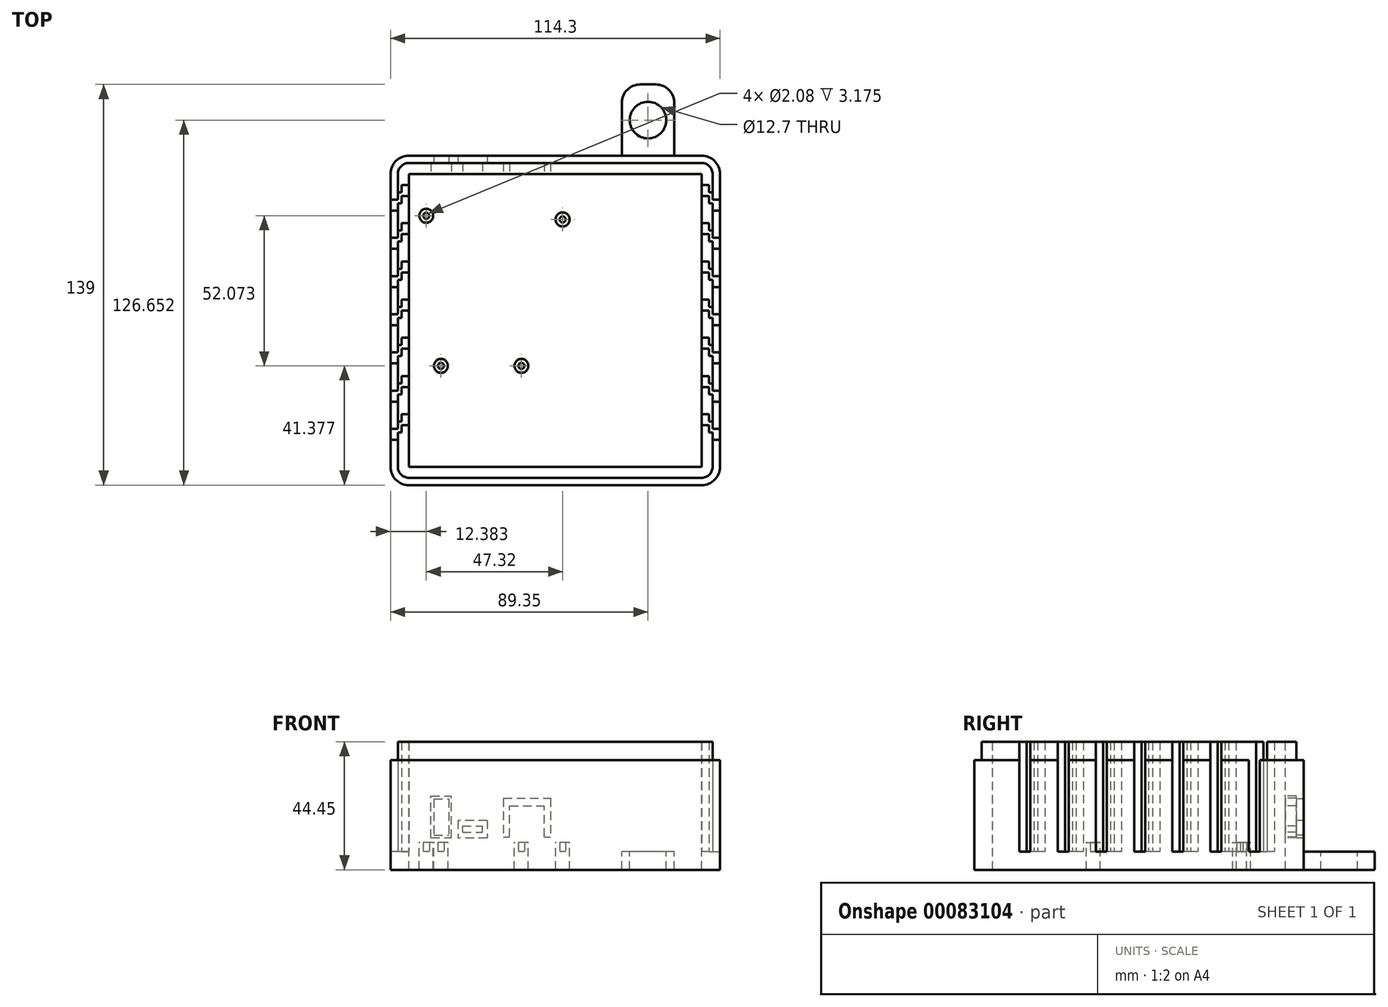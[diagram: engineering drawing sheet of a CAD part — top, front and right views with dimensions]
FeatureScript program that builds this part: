
annotation { "Feature Type Name" : "Feature", "Feature Type Description" : "" }
export const myFeature = defineFeature(function(context is Context, id is Id, definition is map)
    precondition{}
    {
        {
            var Q0;
            Q0=qCreatedBy(makeId("Top.planeOp"),FACE);
            var sketch = newSketch(context, id + "F0", { "sketchPlane" : qUnion([Q0])});
            skLineSegment(sketch, "E0.bottom", {"start": v(50.8, 57.15) * mm, "end": v(-50.8, 57.15) * mm});
            skLineSegment(sketch, "E0.top", {"start": v(50.8, -57.15) * mm, "end": v(-50.8, -57.15) * mm});
            skLineSegment(sketch, "E0.left", {"start": v(57.15, 50.8) * mm, "end": v(57.15, -50.8) * mm});
            skLineSegment(sketch, "E0.right", {"start": v(-57.15, 50.8) * mm, "end": v(-57.15, -50.8) * mm});
            skPoint(sketch, "E0.middle", {"position": v(0, 0) * mm});
            skPoint(sketch, "E1.visualSharp", {"position": v(57.15, 57.15) * mm});
            skArc(sketch, "E1.filletArc", {"start": v(57.15, 50.8) * mm, "mid": v(55.3, 55.3) * mm, "end": v(50.8, 57.15) * mm});
            skPoint(sketch, "E2.visualSharp", {"position": v(57.15, -57.15) * mm});
            skArc(sketch, "E2.filletArc", {"start": v(50.8, -57.15) * mm, "mid": v(55.3, -55.3) * mm, "end": v(57.15, -50.8) * mm});
            skPoint(sketch, "E3.visualSharp", {"position": v(-57.15, -57.15) * mm});
            skArc(sketch, "E3.filletArc", {"start": v(-57.15, -50.8) * mm, "mid": v(-55.3, -55.3) * mm, "end": v(-50.8, -57.15) * mm});
            skPoint(sketch, "E4.visualSharp", {"position": v(-57.15, 57.15) * mm});
            skArc(sketch, "E4.filletArc", {"start": v(-50.8, 57.15) * mm, "mid": v(-55.3, 55.3) * mm, "end": v(-57.15, 50.8) * mm});
            skLineSegment(sketch, "E5.bottom", {"start": v(-50.8, 50.8) * mm, "end": v(50.8, 50.8) * mm});
            skLineSegment(sketch, "E5.top", {"start": v(-50.8, -50.8) * mm, "end": v(50.8, -50.8) * mm});
            skLineSegment(sketch, "E5.left", {"start": v(-50.8, 50.8) * mm, "end": v(-50.8, -50.8) * mm});
            skLineSegment(sketch, "E5.right", {"start": v(50.8, 50.8) * mm, "end": v(50.8, -50.8) * mm});
            skCircle(sketch, "E6", {"center": v(32.2, 69.5) * mm, "radius": 6.35 * mm});
            skLineSegment(sketch, "E7.bottom", {"start": v(41.28, 57.15) * mm, "end": v(23.12, 57.15) * mm});
            skLineSegment(sketch, "E7.top", {"start": v(34.93, 81.85) * mm, "end": v(29.47, 81.85) * mm});
            skLineSegment(sketch, "E7.left", {"start": v(41.28, 57.15) * mm, "end": v(41.28, 75.5) * mm});
            skLineSegment(sketch, "E7.right", {"start": v(23.12, 57.15) * mm, "end": v(23.12, 75.5) * mm});
            skPoint(sketch, "E8.visualSharp", {"position": v(23.12, 81.85) * mm});
            skArc(sketch, "E8.filletArc", {"start": v(29.47, 81.85) * mm, "mid": v(24.98, 80) * mm, "end": v(23.12, 75.5) * mm});
            skPoint(sketch, "E9.visualSharp", {"position": v(41.28, 81.85) * mm});
            skArc(sketch, "E9.filletArc", {"start": v(41.28, 75.5) * mm, "mid": v(39.42, 80) * mm, "end": v(34.93, 81.85) * mm});
            skLineSegment(sketch, "E10.bottom", {"start": v(23.12, 57.15) * mm, "end": v(41.28, 57.15) * mm});
            skLineSegment(sketch, "E10.top", {"start": v(23.12, 50.8) * mm, "end": v(41.28, 50.8) * mm});
            skLineSegment(sketch, "E10.left", {"start": v(23.12, 57.15) * mm, "end": v(23.12, 50.8) * mm});
            skLineSegment(sketch, "E10.right", {"start": v(41.28, 57.15) * mm, "end": v(41.28, 50.8) * mm});
            skLineSegment(sketch, "E11.MirrorCS", {"start": v(23.12, -57.15) * mm, "end": v(23.12, -75.5) * mm});
            skArc(sketch, "E12.MirrorCS", {"start": v(29.47, -81.85) * mm, "mid": v(24.98, -80) * mm, "end": v(23.12, -75.5) * mm});
            skCircle(sketch, "E13.MirrorC", {"center": v(32.2, -69.5) * mm, "radius": 6.35 * mm});
            skLineSegment(sketch, "E14.MirrorCS", {"start": v(23.12, -57.15) * mm, "end": v(23.12, -50.8) * mm});
            skLineSegment(sketch, "E15.MirrorCS", {"start": v(41.28, -57.15) * mm, "end": v(41.28, -50.8) * mm});
            skLineSegment(sketch, "E16.MirrorCS", {"start": v(41.28, -57.15) * mm, "end": v(41.28, -75.5) * mm});
            skArc(sketch, "E17.MirrorCS", {"start": v(41.28, -75.5) * mm, "mid": v(39.42, -80) * mm, "end": v(34.93, -81.85) * mm});
            skLineSegment(sketch, "E18.MirrorCS", {"start": v(34.93, -81.85) * mm, "end": v(29.47, -81.85) * mm});
            skLineSegment(sketch, "E19", {"start": v(-50.8, 47.02) * mm, "end": v(-53.34, 47.02) * mm});
            skLineSegment(sketch, "E20", {"start": v(-53.34, 47.02) * mm, "end": v(-53.34, 44.48) * mm});
            skLineSegment(sketch, "E21", {"start": v(-53.34, 44.48) * mm, "end": v(-54.61, 44.48) * mm});
            skLineSegment(sketch, "E22", {"start": v(-54.61, 44.48) * mm, "end": v(-54.61, 41.94) * mm});
            skLineSegment(sketch, "E23", {"start": v(-54.61, 41.94) * mm, "end": v(-57.15, 41.94) * mm});
            skLineSegment(sketch, "E24", {"start": v(-50.8, 43.21) * mm, "end": v(-53.34, 43.21) * mm});
            skLineSegment(sketch, "E25", {"start": v(-53.34, 43.21) * mm, "end": v(-53.34, 40.67) * mm});
            skLineSegment(sketch, "E26", {"start": v(-53.34, 40.67) * mm, "end": v(-54.6, 40.67) * mm});
            skLineSegment(sketch, "E27", {"start": v(-54.6, 40.67) * mm, "end": v(-54.6, 38.13) * mm});
            skLineSegment(sketch, "E28", {"start": v(-54.6, 38.13) * mm, "end": v(-57.15, 38.13) * mm});
            skLineSegment(sketch, "E29.1.0.0", {"start": v(-53.34, 33.75) * mm, "end": v(-53.34, 31.21) * mm});
            skLineSegment(sketch, "E29.1.0.1", {"start": v(-53.34, 31.21) * mm, "end": v(-54.6, 31.21) * mm});
            skLineSegment(sketch, "E29.1.0.2", {"start": v(-54.6, 31.21) * mm, "end": v(-54.6, 28.67) * mm});
            skLineSegment(sketch, "E29.1.0.3", {"start": v(-53.34, 29.94) * mm, "end": v(-53.34, 27.4) * mm});
            skLineSegment(sketch, "E29.1.0.4", {"start": v(-53.34, 27.4) * mm, "end": v(-54.6, 27.4) * mm});
            skLineSegment(sketch, "E29.1.0.5", {"start": v(-54.6, 27.4) * mm, "end": v(-54.6, 24.86) * mm});
            skLineSegment(sketch, "E29.2.0.0", {"start": v(-53.34, 20.49) * mm, "end": v(-53.34, 17.95) * mm});
            skLineSegment(sketch, "E29.2.0.1", {"start": v(-53.34, 17.95) * mm, "end": v(-54.6, 17.95) * mm});
            skLineSegment(sketch, "E29.2.0.2", {"start": v(-54.6, 17.95) * mm, "end": v(-54.6, 15.4) * mm});
            skLineSegment(sketch, "E29.2.0.3", {"start": v(-53.34, 16.68) * mm, "end": v(-53.34, 14.14) * mm});
            skLineSegment(sketch, "E29.2.0.4", {"start": v(-53.34, 14.14) * mm, "end": v(-54.6, 14.14) * mm});
            skLineSegment(sketch, "E29.2.0.5", {"start": v(-54.6, 14.14) * mm, "end": v(-54.6, 11.6) * mm});
            skLineSegment(sketch, "E29.3.0.0", {"start": v(-53.33, 7.22) * mm, "end": v(-53.33, 4.68) * mm});
            skLineSegment(sketch, "E29.3.0.1", {"start": v(-53.33, 4.68) * mm, "end": v(-54.6, 4.68) * mm});
            skLineSegment(sketch, "E29.3.0.2", {"start": v(-54.6, 4.68) * mm, "end": v(-54.6, 2.14) * mm});
            skLineSegment(sketch, "E29.3.0.3", {"start": v(-53.33, 3.4) * mm, "end": v(-53.33, 0.87) * mm});
            skLineSegment(sketch, "E29.3.0.4", {"start": v(-53.33, 0.87) * mm, "end": v(-54.6, 0.87) * mm});
            skLineSegment(sketch, "E29.3.0.5", {"start": v(-54.6, 0.87) * mm, "end": v(-54.6, -1.67) * mm});
            skLineSegment(sketch, "E29.4.0.0", {"start": v(-53.33, -6.05) * mm, "end": v(-53.33, -8.6) * mm});
            skLineSegment(sketch, "E29.4.0.1", {"start": v(-53.33, -8.6) * mm, "end": v(-54.6, -8.6) * mm});
            skLineSegment(sketch, "E29.4.0.2", {"start": v(-54.6, -8.6) * mm, "end": v(-54.6, -11.13) * mm});
            skLineSegment(sketch, "E29.4.0.3", {"start": v(-53.33, -9.86) * mm, "end": v(-53.33, -12.4) * mm});
            skLineSegment(sketch, "E29.4.0.4", {"start": v(-53.33, -12.4) * mm, "end": v(-54.6, -12.4) * mm});
            skLineSegment(sketch, "E29.4.0.5", {"start": v(-54.6, -12.4) * mm, "end": v(-54.6, -14.94) * mm});
            skLineSegment(sketch, "E29.5.0.0", {"start": v(-53.33, -19.32) * mm, "end": v(-53.33, -21.86) * mm});
            skLineSegment(sketch, "E29.5.0.1", {"start": v(-53.33, -21.86) * mm, "end": v(-54.6, -21.86) * mm});
            skLineSegment(sketch, "E29.5.0.2", {"start": v(-54.6, -21.86) * mm, "end": v(-54.6, -24.4) * mm});
            skLineSegment(sketch, "E29.5.0.3", {"start": v(-53.33, -23.13) * mm, "end": v(-53.33, -25.67) * mm});
            skLineSegment(sketch, "E29.5.0.4", {"start": v(-53.33, -25.67) * mm, "end": v(-54.6, -25.67) * mm});
            skLineSegment(sketch, "E29.5.0.5", {"start": v(-54.6, -25.67) * mm, "end": v(-54.6, -28.2) * mm});
            skLineSegment(sketch, "E29.6.0.0", {"start": v(-53.33, -32.59) * mm, "end": v(-53.33, -35.13) * mm});
            skLineSegment(sketch, "E29.6.0.1", {"start": v(-53.33, -35.13) * mm, "end": v(-54.6, -35.13) * mm});
            skLineSegment(sketch, "E29.6.0.2", {"start": v(-54.6, -35.13) * mm, "end": v(-54.6, -37.67) * mm});
            skLineSegment(sketch, "E29.6.0.3", {"start": v(-53.33, -36.4) * mm, "end": v(-53.33, -38.94) * mm});
            skLineSegment(sketch, "E29.6.0.4", {"start": v(-53.33, -38.94) * mm, "end": v(-54.6, -38.94) * mm});
            skLineSegment(sketch, "E29.6.0.5", {"start": v(-54.6, -38.94) * mm, "end": v(-54.6, -41.48) * mm});
            skLineSegment(sketch, "E29.direction1", {"start": v(-53.34, 44.48) * mm, "end": v(-53.34, 31.21) * mm, "construction": true});
            skLineSegment(sketch, "E30", {"start": v(-53.34, 33.75) * mm, "end": v(-50.8, 33.75) * mm});
            skLineSegment(sketch, "E31", {"start": v(-53.34, 29.94) * mm, "end": v(-50.8, 29.94) * mm});
            skLineSegment(sketch, "E32", {"start": v(-54.6, 28.67) * mm, "end": v(-57.15, 28.67) * mm});
            skLineSegment(sketch, "E33", {"start": v(-54.6, 24.86) * mm, "end": v(-57.15, 24.86) * mm});
            skLineSegment(sketch, "E34", {"start": v(-53.34, 20.49) * mm, "end": v(-50.8, 20.49) * mm});
            skLineSegment(sketch, "E35", {"start": v(-53.34, 16.68) * mm, "end": v(-50.8, 16.68) * mm});
            skLineSegment(sketch, "E36", {"start": v(-54.6, 15.4) * mm, "end": v(-57.15, 15.4) * mm});
            skLineSegment(sketch, "E37", {"start": v(-54.6, 11.6) * mm, "end": v(-57.15, 11.6) * mm});
            skLineSegment(sketch, "E38", {"start": v(-53.33, 7.22) * mm, "end": v(-50.8, 7.22) * mm});
            skLineSegment(sketch, "E39", {"start": v(-53.33, 3.4) * mm, "end": v(-50.8, 3.4) * mm});
            skLineSegment(sketch, "E40", {"start": v(-54.6, 2.14) * mm, "end": v(-57.15, 2.14) * mm});
            skLineSegment(sketch, "E41", {"start": v(-54.6, -1.67) * mm, "end": v(-57.15, -1.67) * mm});
            skLineSegment(sketch, "E42", {"start": v(-53.33, -6.05) * mm, "end": v(-50.8, -6.05) * mm});
            skLineSegment(sketch, "E43", {"start": v(-53.33, -9.86) * mm, "end": v(-50.8, -9.86) * mm});
            skLineSegment(sketch, "E44", {"start": v(-53.33, -19.32) * mm, "end": v(-50.8, -19.32) * mm});
            skLineSegment(sketch, "E45", {"start": v(-53.33, -23.13) * mm, "end": v(-50.8, -23.13) * mm});
            skLineSegment(sketch, "E46", {"start": v(-53.33, -32.59) * mm, "end": v(-50.8, -32.59) * mm});
            skLineSegment(sketch, "E47", {"start": v(-53.33, -36.4) * mm, "end": v(-50.8, -36.4) * mm});
            skLineSegment(sketch, "E48", {"start": v(-54.6, -11.13) * mm, "end": v(-57.15, -11.13) * mm});
            skLineSegment(sketch, "E49", {"start": v(-54.6, -14.94) * mm, "end": v(-57.15, -14.94) * mm});
            skLineSegment(sketch, "E50", {"start": v(-54.6, -24.4) * mm, "end": v(-57.15, -24.4) * mm});
            skLineSegment(sketch, "E51", {"start": v(-54.6, -28.2) * mm, "end": v(-57.15, -28.2) * mm});
            skLineSegment(sketch, "E52", {"start": v(-54.6, -37.67) * mm, "end": v(-57.15, -37.67) * mm});
            skLineSegment(sketch, "E53", {"start": v(-54.6, -41.48) * mm, "end": v(-57.15, -41.48) * mm});
            skLineSegment(sketch, "E54.MirrorCS", {"start": v(54.6, -38.94) * mm, "end": v(54.6, -41.48) * mm});
            skLineSegment(sketch, "E55.MirrorCS", {"start": v(53.33, -38.94) * mm, "end": v(54.6, -38.94) * mm});
            skLineSegment(sketch, "E56.MirrorCS", {"start": v(53.33, -36.4) * mm, "end": v(53.33, -38.94) * mm});
            skLineSegment(sketch, "E57.MirrorCS", {"start": v(54.6, -35.13) * mm, "end": v(54.6, -37.67) * mm});
            skLineSegment(sketch, "E58.MirrorCS", {"start": v(53.33, -35.13) * mm, "end": v(54.6, -35.13) * mm});
            skLineSegment(sketch, "E59.MirrorCS", {"start": v(53.33, -32.59) * mm, "end": v(53.33, -35.13) * mm});
            skLineSegment(sketch, "E60.MirrorCS", {"start": v(54.6, -25.67) * mm, "end": v(54.6, -28.2) * mm});
            skLineSegment(sketch, "E61.MirrorCS", {"start": v(53.33, -25.67) * mm, "end": v(54.6, -25.67) * mm});
            skLineSegment(sketch, "E62.MirrorCS", {"start": v(53.33, -23.13) * mm, "end": v(53.33, -25.67) * mm});
            skLineSegment(sketch, "E63.MirrorCS", {"start": v(54.6, -21.86) * mm, "end": v(54.6, -24.4) * mm});
            skLineSegment(sketch, "E64.MirrorCS", {"start": v(53.33, -21.86) * mm, "end": v(54.6, -21.86) * mm});
            skLineSegment(sketch, "E65.MirrorCS", {"start": v(53.33, -19.32) * mm, "end": v(53.33, -21.86) * mm});
            skLineSegment(sketch, "E66.MirrorCS", {"start": v(54.6, -12.4) * mm, "end": v(54.6, -14.94) * mm});
            skLineSegment(sketch, "E67.MirrorCS", {"start": v(53.33, -12.4) * mm, "end": v(54.6, -12.4) * mm});
            skLineSegment(sketch, "E68.MirrorCS", {"start": v(53.33, -9.86) * mm, "end": v(53.33, -12.4) * mm});
            skLineSegment(sketch, "E69.MirrorCS", {"start": v(54.6, -8.6) * mm, "end": v(54.6, -11.13) * mm});
            skLineSegment(sketch, "E70.MirrorCS", {"start": v(53.33, -8.6) * mm, "end": v(54.6, -8.6) * mm});
            skLineSegment(sketch, "E71.MirrorCS", {"start": v(53.33, -6.05) * mm, "end": v(53.33, -8.6) * mm});
            skLineSegment(sketch, "E72.MirrorCS", {"start": v(54.6, 0.87) * mm, "end": v(54.6, -1.67) * mm});
            skLineSegment(sketch, "E73.MirrorCS", {"start": v(53.33, 0.87) * mm, "end": v(54.6, 0.87) * mm});
            skLineSegment(sketch, "E74.MirrorCS", {"start": v(53.33, 3.4) * mm, "end": v(53.33, 0.87) * mm});
            skLineSegment(sketch, "E75.MirrorCS", {"start": v(54.6, 4.68) * mm, "end": v(54.6, 2.14) * mm});
            skLineSegment(sketch, "E76.MirrorCS", {"start": v(53.33, 4.68) * mm, "end": v(54.6, 4.68) * mm});
            skLineSegment(sketch, "E77.MirrorCS", {"start": v(53.33, 7.22) * mm, "end": v(53.33, 4.68) * mm});
            skLineSegment(sketch, "E78.MirrorCS", {"start": v(53.34, 44.48) * mm, "end": v(54.61, 44.48) * mm});
            skLineSegment(sketch, "E79.MirrorCS", {"start": v(54.61, 44.48) * mm, "end": v(54.61, 41.94) * mm});
            skLineSegment(sketch, "E80.MirrorCS", {"start": v(54.6, 40.67) * mm, "end": v(54.6, 38.13) * mm});
            skLineSegment(sketch, "E81.MirrorCS", {"start": v(53.34, 40.67) * mm, "end": v(54.6, 40.67) * mm});
            skLineSegment(sketch, "E82.MirrorCS", {"start": v(53.34, 43.21) * mm, "end": v(53.34, 40.67) * mm});
            skLineSegment(sketch, "E83.MirrorCS", {"start": v(53.34, 47.02) * mm, "end": v(53.34, 44.48) * mm});
            skLineSegment(sketch, "E84.MirrorCS", {"start": v(54.6, 14.14) * mm, "end": v(54.6, 11.6) * mm});
            skLineSegment(sketch, "E85.MirrorCS", {"start": v(53.34, 14.14) * mm, "end": v(54.6, 14.14) * mm});
            skLineSegment(sketch, "E86.MirrorCS", {"start": v(53.34, 16.68) * mm, "end": v(53.34, 14.14) * mm});
            skLineSegment(sketch, "E87.MirrorCS", {"start": v(54.6, 17.95) * mm, "end": v(54.6, 15.4) * mm});
            skLineSegment(sketch, "E88.MirrorCS", {"start": v(53.34, 17.95) * mm, "end": v(54.6, 17.95) * mm});
            skLineSegment(sketch, "E89.MirrorCS", {"start": v(53.34, 20.49) * mm, "end": v(53.34, 17.95) * mm});
            skLineSegment(sketch, "E90.MirrorCS", {"start": v(54.6, 27.4) * mm, "end": v(54.6, 24.86) * mm});
            skLineSegment(sketch, "E91.MirrorCS", {"start": v(53.34, 27.4) * mm, "end": v(54.6, 27.4) * mm});
            skLineSegment(sketch, "E92.MirrorCS", {"start": v(54.6, 31.21) * mm, "end": v(54.6, 28.67) * mm});
            skLineSegment(sketch, "E93.MirrorCS", {"start": v(53.34, 31.21) * mm, "end": v(54.6, 31.21) * mm});
            skLineSegment(sketch, "E94.MirrorCS", {"start": v(53.34, 29.94) * mm, "end": v(53.34, 27.4) * mm});
            skLineSegment(sketch, "E95.MirrorCS", {"start": v(53.34, 33.75) * mm, "end": v(53.34, 31.21) * mm});
            skLineSegment(sketch, "E96", {"start": v(53.34, 47.02) * mm, "end": v(50.8, 47.02) * mm});
            skLineSegment(sketch, "E97", {"start": v(53.34, 43.21) * mm, "end": v(50.8, 43.21) * mm});
            skLineSegment(sketch, "E98", {"start": v(54.61, 41.94) * mm, "end": v(57.15, 41.94) * mm});
            skLineSegment(sketch, "E99", {"start": v(54.6, 38.13) * mm, "end": v(57.15, 38.13) * mm});
            skLineSegment(sketch, "E100", {"start": v(53.34, 29.94) * mm, "end": v(50.8, 29.94) * mm});
            skLineSegment(sketch, "E101", {"start": v(54.6, 24.86) * mm, "end": v(57.15, 24.86) * mm});
            skLineSegment(sketch, "E102", {"start": v(53.34, 20.49) * mm, "end": v(50.8, 20.49) * mm});
            skLineSegment(sketch, "E103", {"start": v(53.34, 16.68) * mm, "end": v(50.8, 16.68) * mm});
            skLineSegment(sketch, "E104", {"start": v(54.6, 15.4) * mm, "end": v(57.15, 15.4) * mm});
            skLineSegment(sketch, "E105", {"start": v(54.6, 11.6) * mm, "end": v(57.15, 11.6) * mm});
            skLineSegment(sketch, "E106", {"start": v(53.33, 7.22) * mm, "end": v(50.8, 7.22) * mm});
            skLineSegment(sketch, "E107", {"start": v(53.33, 3.4) * mm, "end": v(50.8, 3.4) * mm});
            skLineSegment(sketch, "E108", {"start": v(54.6, 2.14) * mm, "end": v(57.15, 2.14) * mm});
            skLineSegment(sketch, "E109", {"start": v(54.6, -1.67) * mm, "end": v(57.15, -1.67) * mm});
            skLineSegment(sketch, "E110", {"start": v(53.33, -6.05) * mm, "end": v(50.8, -6.05) * mm});
            skLineSegment(sketch, "E111", {"start": v(53.33, -9.86) * mm, "end": v(50.8, -9.86) * mm});
            skLineSegment(sketch, "E112", {"start": v(54.6, -11.13) * mm, "end": v(57.15, -11.13) * mm});
            skLineSegment(sketch, "E113", {"start": v(54.6, -14.94) * mm, "end": v(57.15, -14.94) * mm});
            skLineSegment(sketch, "E114", {"start": v(53.33, -19.32) * mm, "end": v(50.8, -19.32) * mm});
            skLineSegment(sketch, "E115", {"start": v(53.33, -23.13) * mm, "end": v(50.8, -23.13) * mm});
            skLineSegment(sketch, "E116", {"start": v(54.6, -24.4) * mm, "end": v(57.15, -24.4) * mm});
            skLineSegment(sketch, "E117", {"start": v(54.6, -28.2) * mm, "end": v(57.15, -28.2) * mm});
            skLineSegment(sketch, "E118", {"start": v(53.33, -32.59) * mm, "end": v(50.8, -32.59) * mm});
            skLineSegment(sketch, "E119", {"start": v(53.33, -36.4) * mm, "end": v(50.8, -36.4) * mm});
            skLineSegment(sketch, "E120", {"start": v(54.6, -37.67) * mm, "end": v(57.15, -37.67) * mm});
            skLineSegment(sketch, "E121", {"start": v(54.6, -41.48) * mm, "end": v(57.15, -41.48) * mm});
            skLineSegment(sketch, "E122", {"start": v(53.34, 33.75) * mm, "end": v(50.8, 33.75) * mm});
            skLineSegment(sketch, "E123", {"start": v(54.6, 28.67) * mm, "end": v(57.15, 28.67) * mm});
            skLineSegment(sketch, "E124", {"start": v(54.61, -50.8) * mm, "end": v(54.61, 50.8) * mm});
            skLineSegment(sketch, "E125", {"start": v(-54.61, -50.8) * mm, "end": v(-54.61, 50.8) * mm});
            skLineSegment(sketch, "E126", {"start": v(-50.8, 54.61) * mm, "end": v(50.8, 54.61) * mm});
            skArc(sketch, "E127", {"start": v(-50.8, 54.6) * mm, "mid": v(-53.5, 53.5) * mm, "end": v(-54.61, 50.8) * mm});
            skArc(sketch, "E128", {"start": v(50.8, 54.61) * mm, "mid": v(53.5, 53.5) * mm, "end": v(54.6, 50.8) * mm});
            skArc(sketch, "E129", {"start": v(54.61, -50.8) * mm, "mid": v(53.5, -53.5) * mm, "end": v(50.8, -54.61) * mm});
            skArc(sketch, "E130", {"start": v(-54.61, -50.8) * mm, "mid": v(-53.5, -53.5) * mm, "end": v(-50.8, -54.61) * mm});
            skLineSegment(sketch, "E131", {"start": v(-50.8, -54.61) * mm, "end": v(50.8, -54.61) * mm});
            skCircle(sketch, "E132", {"center": v(-44.77, 36.3) * mm, "radius": 1.04 * mm});
            skCircle(sketch, "E133", {"center": v(-44.77, 36.3) * mm, "radius": 2.42 * mm});
            skCircle(sketch, "E134", {"center": v(2.55, 35.03) * mm, "radius": 1.04 * mm});
            skCircle(sketch, "E135", {"center": v(2.55, 35.03) * mm, "radius": 2.42 * mm});
            skCircle(sketch, "E136", {"center": v(-39.67, -15.77) * mm, "radius": 1.04 * mm});
            skCircle(sketch, "E137", {"center": v(-39.67, -15.77) * mm, "radius": 2.42 * mm});
            skCircle(sketch, "E138", {"center": v(-11.73, -15.77) * mm, "radius": 1.04 * mm});
            skCircle(sketch, "E139", {"center": v(-11.73, -15.77) * mm, "radius": 2.42 * mm});
            skSolve(sketch);
        }
        {
            var Q0;
            {var subQ5=sQuery(id+"F0.wireOp",EDGE,"E4.filletArc");Q0=makeQuery(id+"F0.imprint","IMPRINT",FACE,{"disambiguationData":[TD([[makeQuery(id+"F0.imprint","IMPRINT",EDGE,{"derivedFrom":subQ5}),1.0]])]});}
            var Q1;
            {var subQ0=sQuery(id+"F0.wireOp",EDGE,"E19");Q1=makeQuery(id+"F0.imprint","IMPRINT",FACE,{"disambiguationData":[TD([[makeQuery(id+"F0.imprint","IMPRINT",EDGE,{"derivedFrom":subQ0}),-1.0]])]});}
            var Q2;
            {var subQ0=sQuery(id+"F0.wireOp",EDGE,"7fccda47-ab33-4617-952b-09ef6f2d93c20.MirrorCS");var subQ1=sQuery(id+"F0.wireOp",EDGE,"E5.bottom");var subQ2=makeQuery(id+"F0.imprint","INTERSECT",VERTEX,{"derivedFrom":[subQ1,subQ0]});Q2=makeQuery(id+"F0.imprint","IMPRINT",FACE,{"disambiguationData":[TD([[makeQuery(id+"F0.imprint","IMPRINT",EDGE,{"disambiguationData":[TD([[subQ2,1.0]])],"derivedFrom":subQ1}),1.0]])]});}
            var Q3;
            {var subQ0=sQuery(id+"F0.wireOp",EDGE,"7fccda47-ab33-4617-952b-09ef6f2d93c20.MirrorCS");var subQ5=sQuery(id+"F0.wireOp",EDGE,"E126");var subQ6=makeQuery(id+"F0.imprint","INTERSECT",VERTEX,{"derivedFrom":[subQ0,subQ5]});Q3=makeQuery(id+"F0.imprint","IMPRINT",FACE,{"disambiguationData":[TD([[makeQuery(id+"F0.imprint","IMPRINT",EDGE,{"disambiguationData":[TD([[subQ6,1.0]])],"derivedFrom":subQ5}),1.0]])]});}
            var Q4;
            {var subQ1=sQuery(id+"F0.wireOp",EDGE,"f4708bc4-65f7-4d25-ab76-2e2c8adc8cc10.MirrorCS");Q4=makeQuery(id+"F0.imprint","IMPRINT",FACE,{"disambiguationData":[TD([[makeQuery(id+"F0.imprint","IMPRINT",EDGE,{"derivedFrom":subQ1}),1.0]])]});}
            var Q5;
            {var subQ0=sQuery(id+"F0.wireOp",EDGE,"E10.left");var subQ5=sQuery(id+"F0.wireOp",EDGE,"E126");var subQ6=makeQuery(id+"F0.imprint","INTERSECT",VERTEX,{"derivedFrom":[subQ0,subQ5]});Q5=makeQuery(id+"F0.imprint","IMPRINT",FACE,{"disambiguationData":[TD([[makeQuery(id+"F0.imprint","IMPRINT",EDGE,{"disambiguationData":[TD([[subQ6,1.0]])],"derivedFrom":subQ5}),1.0]])]});}
            var Q6;
            {var subQ1=sQuery(id+"F0.wireOp",EDGE,"E5.bottom");var subQ3=sQuery(id+"F0.wireOp",EDGE,"7fccda47-ab33-4617-952b-09ef6f2d93c20.MirrorCS");var subQ4=makeQuery(id+"F0.imprint","INTERSECT",VERTEX,{"derivedFrom":[subQ1,subQ3]});Q6=makeQuery(id+"F0.imprint","IMPRINT",FACE,{"disambiguationData":[TD([[makeQuery(id+"F0.imprint","IMPRINT",EDGE,{"disambiguationData":[TD([[subQ4,1.0]])],"derivedFrom":subQ3}),1.0]])]});}
            var Q7;
            {var subQ0=sQuery(id+"F0.wireOp",EDGE,"E10.top");Q7=makeQuery(id+"F0.imprint","IMPRINT",FACE,{"disambiguationData":[TD([[makeQuery(id+"F0.imprint","IMPRINT",EDGE,{"derivedFrom":subQ0}),1.0]])]});}
            var Q8;
            {var subQ0=sQuery(id+"F0.wireOp",EDGE,"E10.bottom");Q8=makeQuery(id+"F0.imprint","IMPRINT",FACE,{"disambiguationData":[TD([[makeQuery(id+"F0.imprint","IMPRINT",EDGE,{"derivedFrom":subQ0}),-1.0]])]});}
            var Q9;
            Q9=makeQuery(id+"F0.imprint","IMPRINT",FACE,{"disambiguationData":[TD([[makeQuery(id+"F0.imprint","IMPRINT",EDGE,{"derivedFrom":sQuery(id+"F0.wireOp",EDGE,"E6")}),-1.0]])]});
            var Q10;
            {var subQ8=sQuery(id+"F0.wireOp",EDGE,"E1.filletArc");Q10=makeQuery(id+"F0.imprint","IMPRINT",FACE,{"disambiguationData":[TD([[makeQuery(id+"F0.imprint","IMPRINT",EDGE,{"derivedFrom":subQ8}),1.0]])]});}
            var Q11;
            Q11=makeQuery(id+"F0.imprint","IMPRINT",FACE,{"disambiguationData":[TD([[makeQuery(id+"F0.imprint","IMPRINT",EDGE,{"derivedFrom":sQuery(id+"F0.wireOp",EDGE,"E83.MirrorCS")}),1.0]])]});
            var Q12;
            Q12=makeQuery(id+"F0.imprint","IMPRINT",FACE,{"disambiguationData":[TD([[makeQuery(id+"F0.imprint","IMPRINT",EDGE,{"derivedFrom":sQuery(id+"F0.wireOp",EDGE,"E83.MirrorCS")}),-1.0]])]});
            var Q13;
            {var subQ3=sQuery(id+"F0.wireOp",EDGE,"E98");Q13=makeQuery(id+"F0.imprint","IMPRINT",FACE,{"disambiguationData":[TD([[makeQuery(id+"F0.imprint","IMPRINT",EDGE,{"derivedFrom":subQ3}),-1.0]])]});}
            var Q14;
            {var subQ0=sQuery(id+"F0.wireOp",EDGE,"E99");Q14=makeQuery(id+"F0.imprint","IMPRINT",FACE,{"disambiguationData":[TD([[makeQuery(id+"F0.imprint","IMPRINT",EDGE,{"derivedFrom":subQ0}),-1.0]])]});}
            var Q15;
            Q15=makeQuery(id+"F0.imprint","IMPRINT",FACE,{"disambiguationData":[TD([[makeQuery(id+"F0.imprint","IMPRINT",EDGE,{"derivedFrom":sQuery(id+"F0.wireOp",EDGE,"E82.MirrorCS")}),-1.0]])]});
            var Q16;
            Q16=makeQuery(id+"F0.imprint","IMPRINT",FACE,{"disambiguationData":[TD([[makeQuery(id+"F0.imprint","IMPRINT",EDGE,{"derivedFrom":sQuery(id+"F0.wireOp",EDGE,"E95.MirrorCS")}),-1.0]])]});
            var Q17;
            {var subQ0=sQuery(id+"F0.wireOp",EDGE,"E101");var subQ1=sQuery(id+"F0.wireOp",EDGE,"E0.left");var subQ2=makeQuery(id+"F0.imprint","INTERSECT",VERTEX,{"derivedFrom":[subQ1,subQ0]});Q17=makeQuery(id+"F0.imprint","IMPRINT",FACE,{"disambiguationData":[TD([[makeQuery(id+"F0.imprint","IMPRINT",EDGE,{"disambiguationData":[TD([[subQ2,1.0]])],"derivedFrom":subQ1}),-1.0]])]});}
            var Q18;
            {var subQ0=sQuery(id+"F0.wireOp",EDGE,"E101");var subQ1=sQuery(id+"F0.wireOp",EDGE,"E0.left");var subQ2=makeQuery(id+"F0.imprint","INTERSECT",VERTEX,{"derivedFrom":[subQ1,subQ0]});Q18=makeQuery(id+"F0.imprint","IMPRINT",FACE,{"disambiguationData":[TD([[makeQuery(id+"F0.imprint","IMPRINT",EDGE,{"disambiguationData":[TD([[subQ2,-1.0]])],"derivedFrom":subQ1}),-1.0]])]});}
            var Q19;
            {var subQ6=sQuery(id+"F0.wireOp",EDGE,"E87.MirrorCS");Q19=makeQuery(id+"F0.imprint","IMPRINT",FACE,{"disambiguationData":[TD([[makeQuery(id+"F0.imprint","IMPRINT",EDGE,{"derivedFrom":subQ6}),1.0]])]});}
            var Q20;
            {var subQ7=sQuery(id+"F0.wireOp",EDGE,"E84.MirrorCS");Q20=makeQuery(id+"F0.imprint","IMPRINT",FACE,{"disambiguationData":[TD([[makeQuery(id+"F0.imprint","IMPRINT",EDGE,{"derivedFrom":subQ7}),1.0]])]});}
            var Q21;
            {var subQ0=sQuery(id+"F0.wireOp",EDGE,"E104");var subQ1=sQuery(id+"F0.wireOp",EDGE,"E0.left");var subQ2=makeQuery(id+"F0.imprint","INTERSECT",VERTEX,{"derivedFrom":[subQ1,subQ0]});Q21=makeQuery(id+"F0.imprint","IMPRINT",FACE,{"disambiguationData":[TD([[makeQuery(id+"F0.imprint","IMPRINT",EDGE,{"disambiguationData":[TD([[subQ2,-1.0]])],"derivedFrom":subQ1}),-1.0]])]});}
            var Q22;
            {var subQ8=sQuery(id+"F0.wireOp",EDGE,"E75.MirrorCS");Q22=makeQuery(id+"F0.imprint","IMPRINT",FACE,{"disambiguationData":[TD([[makeQuery(id+"F0.imprint","IMPRINT",EDGE,{"derivedFrom":subQ8}),1.0]])]});}
            var Q23;
            {var subQ0=sQuery(id+"F0.wireOp",EDGE,"E105");var subQ1=sQuery(id+"F0.wireOp",EDGE,"E0.left");var subQ2=makeQuery(id+"F0.imprint","INTERSECT",VERTEX,{"derivedFrom":[subQ1,subQ0]});Q23=makeQuery(id+"F0.imprint","IMPRINT",FACE,{"disambiguationData":[TD([[makeQuery(id+"F0.imprint","IMPRINT",EDGE,{"disambiguationData":[TD([[subQ2,-1.0]])],"derivedFrom":subQ1}),-1.0]])]});}
            var Q24;
            {var subQ0=sQuery(id+"F0.wireOp",EDGE,"E108");var subQ1=sQuery(id+"F0.wireOp",EDGE,"E0.left");var subQ2=makeQuery(id+"F0.imprint","INTERSECT",VERTEX,{"derivedFrom":[subQ1,subQ0]});Q24=makeQuery(id+"F0.imprint","IMPRINT",FACE,{"disambiguationData":[TD([[makeQuery(id+"F0.imprint","IMPRINT",EDGE,{"disambiguationData":[TD([[subQ2,-1.0]])],"derivedFrom":subQ1}),-1.0]])]});}
            var Q25;
            {var subQ6=sQuery(id+"F0.wireOp",EDGE,"E72.MirrorCS");Q25=makeQuery(id+"F0.imprint","IMPRINT",FACE,{"disambiguationData":[TD([[makeQuery(id+"F0.imprint","IMPRINT",EDGE,{"derivedFrom":subQ6}),1.0]])]});}
            var Q26;
            {var subQ6=sQuery(id+"F0.wireOp",EDGE,"E69.MirrorCS");Q26=makeQuery(id+"F0.imprint","IMPRINT",FACE,{"disambiguationData":[TD([[makeQuery(id+"F0.imprint","IMPRINT",EDGE,{"derivedFrom":subQ6}),1.0]])]});}
            var Q27;
            {var subQ0=sQuery(id+"F0.wireOp",EDGE,"E109");var subQ1=sQuery(id+"F0.wireOp",EDGE,"E0.left");var subQ2=makeQuery(id+"F0.imprint","INTERSECT",VERTEX,{"derivedFrom":[subQ1,subQ0]});Q27=makeQuery(id+"F0.imprint","IMPRINT",FACE,{"disambiguationData":[TD([[makeQuery(id+"F0.imprint","IMPRINT",EDGE,{"disambiguationData":[TD([[subQ2,-1.0]])],"derivedFrom":subQ1}),-1.0]])]});}
            var Q28;
            {var subQ9=sQuery(id+"F0.wireOp",EDGE,"E66.MirrorCS");Q28=makeQuery(id+"F0.imprint","IMPRINT",FACE,{"disambiguationData":[TD([[makeQuery(id+"F0.imprint","IMPRINT",EDGE,{"derivedFrom":subQ9}),1.0]])]});}
            var Q29;
            {var subQ0=sQuery(id+"F0.wireOp",EDGE,"E112");var subQ1=sQuery(id+"F0.wireOp",EDGE,"E0.left");var subQ2=makeQuery(id+"F0.imprint","INTERSECT",VERTEX,{"derivedFrom":[subQ1,subQ0]});Q29=makeQuery(id+"F0.imprint","IMPRINT",FACE,{"disambiguationData":[TD([[makeQuery(id+"F0.imprint","IMPRINT",EDGE,{"disambiguationData":[TD([[subQ2,-1.0]])],"derivedFrom":subQ1}),-1.0]])]});}
            var Q30;
            {var subQ0=sQuery(id+"F0.wireOp",EDGE,"E113");var subQ1=sQuery(id+"F0.wireOp",EDGE,"E0.left");var subQ2=makeQuery(id+"F0.imprint","INTERSECT",VERTEX,{"derivedFrom":[subQ1,subQ0]});Q30=makeQuery(id+"F0.imprint","IMPRINT",FACE,{"disambiguationData":[TD([[makeQuery(id+"F0.imprint","IMPRINT",EDGE,{"disambiguationData":[TD([[subQ2,-1.0]])],"derivedFrom":subQ1}),-1.0]])]});}
            var Q31;
            {var subQ7=sQuery(id+"F0.wireOp",EDGE,"E63.MirrorCS");Q31=makeQuery(id+"F0.imprint","IMPRINT",FACE,{"disambiguationData":[TD([[makeQuery(id+"F0.imprint","IMPRINT",EDGE,{"derivedFrom":subQ7}),1.0]])]});}
            var Q32;
            {var subQ8=sQuery(id+"F0.wireOp",EDGE,"E60.MirrorCS");Q32=makeQuery(id+"F0.imprint","IMPRINT",FACE,{"disambiguationData":[TD([[makeQuery(id+"F0.imprint","IMPRINT",EDGE,{"derivedFrom":subQ8}),1.0]])]});}
            var Q33;
            {var subQ0=sQuery(id+"F0.wireOp",EDGE,"E116");var subQ1=sQuery(id+"F0.wireOp",EDGE,"E0.left");var subQ2=makeQuery(id+"F0.imprint","INTERSECT",VERTEX,{"derivedFrom":[subQ1,subQ0]});Q33=makeQuery(id+"F0.imprint","IMPRINT",FACE,{"disambiguationData":[TD([[makeQuery(id+"F0.imprint","IMPRINT",EDGE,{"disambiguationData":[TD([[subQ2,-1.0]])],"derivedFrom":subQ1}),-1.0]])]});}
            var Q34;
            {var subQ0=sQuery(id+"F0.wireOp",EDGE,"E117");var subQ1=sQuery(id+"F0.wireOp",EDGE,"E0.left");var subQ2=makeQuery(id+"F0.imprint","INTERSECT",VERTEX,{"derivedFrom":[subQ1,subQ0]});Q34=makeQuery(id+"F0.imprint","IMPRINT",FACE,{"disambiguationData":[TD([[makeQuery(id+"F0.imprint","IMPRINT",EDGE,{"disambiguationData":[TD([[subQ2,-1.0]])],"derivedFrom":subQ1}),-1.0]])]});}
            var Q35;
            {var subQ7=sQuery(id+"F0.wireOp",EDGE,"E57.MirrorCS");Q35=makeQuery(id+"F0.imprint","IMPRINT",FACE,{"disambiguationData":[TD([[makeQuery(id+"F0.imprint","IMPRINT",EDGE,{"derivedFrom":subQ7}),1.0]])]});}
            var Q36;
            {var subQ7=sQuery(id+"F0.wireOp",EDGE,"E54.MirrorCS");Q36=makeQuery(id+"F0.imprint","IMPRINT",FACE,{"disambiguationData":[TD([[makeQuery(id+"F0.imprint","IMPRINT",EDGE,{"derivedFrom":subQ7}),1.0]])]});}
            var Q37;
            {var subQ0=sQuery(id+"F0.wireOp",EDGE,"E120");var subQ1=sQuery(id+"F0.wireOp",EDGE,"E0.left");var subQ2=makeQuery(id+"F0.imprint","INTERSECT",VERTEX,{"derivedFrom":[subQ1,subQ0]});Q37=makeQuery(id+"F0.imprint","IMPRINT",FACE,{"disambiguationData":[TD([[makeQuery(id+"F0.imprint","IMPRINT",EDGE,{"disambiguationData":[TD([[subQ2,-1.0]])],"derivedFrom":subQ1}),-1.0]])]});}
            var Q38;
            {var subQ0=sQuery(id+"F0.wireOp",EDGE,"E121");var subQ1=sQuery(id+"F0.wireOp",EDGE,"E0.left");var subQ2=makeQuery(id+"F0.imprint","INTERSECT",VERTEX,{"derivedFrom":[subQ1,subQ0]});Q38=makeQuery(id+"F0.imprint","IMPRINT",FACE,{"disambiguationData":[TD([[makeQuery(id+"F0.imprint","IMPRINT",EDGE,{"disambiguationData":[TD([[subQ2,-1.0]])],"derivedFrom":subQ1}),-1.0]])]});}
            var Q39;
            {var subQ7=sQuery(id+"F0.wireOp",EDGE,"859455d8-9afb-47e5-a04d-dad7f7b3347415.MirrorCS");Q39=makeQuery(id+"F0.imprint","IMPRINT",FACE,{"disambiguationData":[TD([[makeQuery(id+"F0.imprint","IMPRINT",EDGE,{"derivedFrom":subQ7}),1.0]])]});}
            var Q40;
            Q40=makeQuery(id+"F0.imprint","IMPRINT",FACE,{"disambiguationData":[TD([[makeQuery(id+"F0.imprint","IMPRINT",EDGE,{"derivedFrom":sQuery(id+"F0.wireOp",EDGE,"859455d8-9afb-47e5-a04d-dad7f7b3347412.MirrorCS")}),1.0]])]});
            var Q41;
            {var subQ0=sQuery(id+"F0.wireOp",EDGE,"PCcy3vUJ-A1Sm-yILS-TfP7-LZ45dRfwLIWC");var subQ1=sQuery(id+"F0.wireOp",EDGE,"E0.left");var subQ2=makeQuery(id+"F0.imprint","INTERSECT",VERTEX,{"derivedFrom":[subQ1,subQ0]});Q41=makeQuery(id+"F0.imprint","IMPRINT",FACE,{"disambiguationData":[TD([[makeQuery(id+"F0.imprint","IMPRINT",EDGE,{"disambiguationData":[TD([[subQ2,-1.0]])],"derivedFrom":subQ1}),-1.0]])]});}
            var Q42;
            {var subQ3=sQuery(id+"F0.wireOp",EDGE,"859455d8-9afb-47e5-a04d-dad7f7b334749.MirrorCS");Q42=makeQuery(id+"F0.imprint","IMPRINT",FACE,{"disambiguationData":[TD([[makeQuery(id+"F0.imprint","IMPRINT",EDGE,{"derivedFrom":subQ3}),1.0]])]});}
            var Q43;
            {var subQ0=sQuery(id+"F0.wireOp",EDGE,"SMXw2df1-MZSw-PhrQ-Zi49-mZn6oChbaFUW");var subQ1=sQuery(id+"F0.wireOp",EDGE,"E0.left");var subQ2=makeQuery(id+"F0.imprint","INTERSECT",VERTEX,{"derivedFrom":[subQ1,subQ0]});Q43=makeQuery(id+"F0.imprint","IMPRINT",FACE,{"disambiguationData":[TD([[makeQuery(id+"F0.imprint","IMPRINT",EDGE,{"disambiguationData":[TD([[subQ2,-1.0]])],"derivedFrom":subQ1}),-1.0]])]});}
            var Q44;
            {var subQ0=sQuery(id+"F0.wireOp",EDGE,"4gdouP2l-Rrvu-6Vf7-YE6u-t5k5cjv6Sdnn");var subQ1=sQuery(id+"F0.wireOp",EDGE,"E0.left");var subQ2=makeQuery(id+"F0.imprint","INTERSECT",VERTEX,{"derivedFrom":[subQ1,subQ0]});Q44=makeQuery(id+"F0.imprint","IMPRINT",FACE,{"disambiguationData":[TD([[makeQuery(id+"F0.imprint","IMPRINT",EDGE,{"disambiguationData":[TD([[subQ2,-1.0]])],"derivedFrom":subQ1}),-1.0]])]});}
            var Q45;
            {var subQ7=sQuery(id+"F0.wireOp",EDGE,"859455d8-9afb-47e5-a04d-dad7f7b334746.MirrorCS");Q45=makeQuery(id+"F0.imprint","IMPRINT",FACE,{"disambiguationData":[TD([[makeQuery(id+"F0.imprint","IMPRINT",EDGE,{"derivedFrom":subQ7}),1.0]])]});}
            var Q46;
            {var subQ9=sQuery(id+"F0.wireOp",EDGE,"859455d8-9afb-47e5-a04d-dad7f7b334743.MirrorCS");Q46=makeQuery(id+"F0.imprint","IMPRINT",FACE,{"disambiguationData":[TD([[makeQuery(id+"F0.imprint","IMPRINT",EDGE,{"derivedFrom":subQ9}),1.0]])]});}
            var Q47;
            {var subQ0=sQuery(id+"F0.wireOp",EDGE,"YNpdqX5B-PI5h-3Mbl-nZAo-x4syKM0iqF3R");var subQ1=sQuery(id+"F0.wireOp",EDGE,"E0.left");var subQ2=makeQuery(id+"F0.imprint","INTERSECT",VERTEX,{"derivedFrom":[subQ1,subQ0]});Q47=makeQuery(id+"F0.imprint","IMPRINT",FACE,{"disambiguationData":[TD([[makeQuery(id+"F0.imprint","IMPRINT",EDGE,{"disambiguationData":[TD([[subQ2,-1.0]])],"derivedFrom":subQ1}),-1.0]])]});}
            var Q48;
            {var subQ5=sQuery(id+"F0.wireOp",EDGE,"859455d8-9afb-47e5-a04d-dad7f7b334740.MirrorCS");Q48=makeQuery(id+"F0.imprint","IMPRINT",FACE,{"disambiguationData":[TD([[makeQuery(id+"F0.imprint","IMPRINT",EDGE,{"derivedFrom":subQ5}),1.0]])]});}
            var Q49;
            {var subQ0=sQuery(id+"F0.wireOp",EDGE,"0zjqmZ1I-EMqr-o7fn-YuRe-ZU3UoU47uyUz");var subQ1=sQuery(id+"F0.wireOp",EDGE,"E0.left");var subQ2=makeQuery(id+"F0.imprint","INTERSECT",VERTEX,{"derivedFrom":[subQ1,subQ0]});Q49=makeQuery(id+"F0.imprint","IMPRINT",FACE,{"disambiguationData":[TD([[makeQuery(id+"F0.imprint","IMPRINT",EDGE,{"disambiguationData":[TD([[subQ2,-1.0]])],"derivedFrom":subQ1}),-1.0]])]});}
            var Q50;
            {var subQ5=sQuery(id+"F0.wireOp",EDGE,"E2.filletArc");Q50=makeQuery(id+"F0.imprint","IMPRINT",FACE,{"disambiguationData":[TD([[makeQuery(id+"F0.imprint","IMPRINT",EDGE,{"derivedFrom":subQ5}),1.0]])]});}
            var Q51;
            {var subQ4=sQuery(id+"F0.wireOp",EDGE,"859455d8-9afb-47e5-a04d-dad7f7b334740.MirrorCS");Q51=makeQuery(id+"F0.imprint","IMPRINT",FACE,{"disambiguationData":[TD([[makeQuery(id+"F0.imprint","IMPRINT",EDGE,{"derivedFrom":subQ4}),-1.0]])]});}
            var Q52;
            {var subQ0=sQuery(id+"F0.wireOp",EDGE,"E14.MirrorCS");var subQ1=sQuery(id+"F0.wireOp",EDGE,"E5.top");var subQ2=makeQuery(id+"F0.imprint","INTERSECT",VERTEX,{"derivedFrom":[subQ1,subQ0]});Q52=makeQuery(id+"F0.imprint","IMPRINT",FACE,{"disambiguationData":[TD([[makeQuery(id+"F0.imprint","IMPRINT",EDGE,{"disambiguationData":[TD([[subQ2,-1.0]])],"derivedFrom":subQ1}),-1.0]])]});}
            var Q53;
            {var subQ0=sQuery(id+"F0.wireOp",EDGE,"E14.MirrorCS");var subQ5=sQuery(id+"F0.wireOp",EDGE,"E131");var subQ6=makeQuery(id+"F0.imprint","INTERSECT",VERTEX,{"derivedFrom":[subQ0,subQ5]});Q53=makeQuery(id+"F0.imprint","IMPRINT",FACE,{"disambiguationData":[TD([[makeQuery(id+"F0.imprint","IMPRINT",EDGE,{"disambiguationData":[TD([[subQ6,-1.0]])],"derivedFrom":subQ5}),-1.0]])]});}
            var Q54;
            Q54=makeQuery(id+"F0.imprint","IMPRINT",FACE,{"disambiguationData":[TD([[makeQuery(id+"F0.imprint","IMPRINT",EDGE,{"derivedFrom":sQuery(id+"F0.wireOp",EDGE,"E12.MirrorCS")}),-1.0]])]});
            var Q55;
            {var subQ0=sQuery(id+"F0.wireOp",EDGE,"E14.MirrorCS");var subQ1=sQuery(id+"F0.wireOp",EDGE,"E5.top");var subQ2=makeQuery(id+"F0.imprint","INTERSECT",VERTEX,{"derivedFrom":[subQ1,subQ0]});Q55=makeQuery(id+"F0.imprint","IMPRINT",FACE,{"disambiguationData":[TD([[makeQuery(id+"F0.imprint","IMPRINT",EDGE,{"disambiguationData":[TD([[subQ2,1.0]])],"derivedFrom":subQ1}),-1.0]])]});}
            var Q56;
            {var subQ0=sQuery(id+"F0.wireOp",EDGE,"E14.MirrorCS");var subQ5=sQuery(id+"F0.wireOp",EDGE,"E131");var subQ6=makeQuery(id+"F0.imprint","INTERSECT",VERTEX,{"derivedFrom":[subQ0,subQ5]});Q56=makeQuery(id+"F0.imprint","IMPRINT",FACE,{"disambiguationData":[TD([[makeQuery(id+"F0.imprint","IMPRINT",EDGE,{"disambiguationData":[TD([[subQ6,1.0]])],"derivedFrom":subQ5}),-1.0]])]});}
            var Q57;
            {var subQ0=sQuery(id+"F0.wireOp",EDGE,"7ab7f921-5da6-4109-8e3c-2e87eee36be50.MirrorCS");var subQ1=sQuery(id+"F0.wireOp",EDGE,"E5.top");var subQ2=makeQuery(id+"F0.imprint","INTERSECT",VERTEX,{"derivedFrom":[subQ1,subQ0]});Q57=makeQuery(id+"F0.imprint","IMPRINT",FACE,{"disambiguationData":[TD([[makeQuery(id+"F0.imprint","IMPRINT",EDGE,{"disambiguationData":[TD([[subQ2,1.0]])],"derivedFrom":subQ1}),-1.0]])]});}
            var Q58;
            {var subQ0=sQuery(id+"F0.wireOp",EDGE,"7ab7f921-5da6-4109-8e3c-2e87eee36be50.MirrorCS");var subQ5=sQuery(id+"F0.wireOp",EDGE,"E131");var subQ6=makeQuery(id+"F0.imprint","INTERSECT",VERTEX,{"derivedFrom":[subQ0,subQ5]});Q58=makeQuery(id+"F0.imprint","IMPRINT",FACE,{"disambiguationData":[TD([[makeQuery(id+"F0.imprint","IMPRINT",EDGE,{"disambiguationData":[TD([[subQ6,1.0]])],"derivedFrom":subQ5}),-1.0]])]});}
            var Q59;
            {var subQ0=sQuery(id+"F0.wireOp",EDGE,"550fb65e-1ebd-4659-b234-2574456a915c0.MirrorCS");Q59=makeQuery(id+"F0.imprint","IMPRINT",FACE,{"disambiguationData":[TD([[makeQuery(id+"F0.imprint","IMPRINT",EDGE,{"derivedFrom":subQ0}),-1.0]])]});}
            var Q60;
            Q60=makeQuery(id+"F0.imprint","IMPRINT",FACE,{"disambiguationData":[TD([[makeQuery(id+"F0.imprint","IMPRINT",EDGE,{"derivedFrom":sQuery(id+"F0.wireOp",EDGE,"E29.9.0.3")}),1.0]])]});
            var Q61;
            {var subQ5=sQuery(id+"F0.wireOp",EDGE,"E3.filletArc");Q61=makeQuery(id+"F0.imprint","IMPRINT",FACE,{"disambiguationData":[TD([[makeQuery(id+"F0.imprint","IMPRINT",EDGE,{"derivedFrom":subQ5}),1.0]])]});}
            var Q62;
            {var subQ0=sQuery(id+"F0.wireOp",EDGE,"mRmWzv1N-bWcO-9Rz8-5K5q-iSv0tvIejwaz");var subQ1=sQuery(id+"F0.wireOp",EDGE,"E0.right");var subQ2=makeQuery(id+"F0.imprint","INTERSECT",VERTEX,{"derivedFrom":[subQ1,subQ0]});Q62=makeQuery(id+"F0.imprint","IMPRINT",FACE,{"disambiguationData":[TD([[makeQuery(id+"F0.imprint","IMPRINT",EDGE,{"disambiguationData":[TD([[subQ2,1.0]])],"derivedFrom":subQ1}),1.0]])]});}
            var Q63;
            Q63=makeQuery(id+"F0.imprint","IMPRINT",FACE,{"disambiguationData":[TD([[makeQuery(id+"F0.imprint","IMPRINT",EDGE,{"derivedFrom":sQuery(id+"F0.wireOp",EDGE,"E29.9.0.0")}),1.0]])]});
            var Q64;
            {var subQ0=sQuery(id+"F0.wireOp",EDGE,"Qj8Wj7Yq-4zai-SqqA-oXQt-EhOUvbfXBA7m");var subQ1=sQuery(id+"F0.wireOp",EDGE,"E0.right");var subQ2=makeQuery(id+"F0.imprint","INTERSECT",VERTEX,{"derivedFrom":[subQ1,subQ0]});Q64=makeQuery(id+"F0.imprint","IMPRINT",FACE,{"disambiguationData":[TD([[makeQuery(id+"F0.imprint","IMPRINT",EDGE,{"disambiguationData":[TD([[subQ2,-1.0]])],"derivedFrom":subQ1}),1.0]])]});}
            var Q65;
            Q65=makeQuery(id+"F0.imprint","IMPRINT",FACE,{"disambiguationData":[TD([[makeQuery(id+"F0.imprint","IMPRINT",EDGE,{"derivedFrom":sQuery(id+"F0.wireOp",EDGE,"E29.8.0.3")}),1.0]])]});
            var Q66;
            {var subQ0=sQuery(id+"F0.wireOp",EDGE,"vKAd7Xoy-10xO-Qdgf-Dpy4-s2GlEv8SRybZ");var subQ1=sQuery(id+"F0.wireOp",EDGE,"E0.right");var subQ2=makeQuery(id+"F0.imprint","INTERSECT",VERTEX,{"derivedFrom":[subQ1,subQ0]});Q66=makeQuery(id+"F0.imprint","IMPRINT",FACE,{"disambiguationData":[TD([[makeQuery(id+"F0.imprint","IMPRINT",EDGE,{"disambiguationData":[TD([[subQ2,-1.0]])],"derivedFrom":subQ1}),1.0]])]});}
            var Q67;
            Q67=makeQuery(id+"F0.imprint","IMPRINT",FACE,{"disambiguationData":[TD([[makeQuery(id+"F0.imprint","IMPRINT",EDGE,{"derivedFrom":sQuery(id+"F0.wireOp",EDGE,"E29.8.0.0")}),1.0]])]});
            var Q68;
            Q68=makeQuery(id+"F0.imprint","IMPRINT",FACE,{"disambiguationData":[TD([[makeQuery(id+"F0.imprint","IMPRINT",EDGE,{"derivedFrom":sQuery(id+"F0.wireOp",EDGE,"E29.7.0.3")}),1.0]])]});
            var Q69;
            {var subQ0=sQuery(id+"F0.wireOp",EDGE,"rDNda6TP-Z5lF-aWdB-fPSw-GyjD0bS7NVlS");var subQ1=sQuery(id+"F0.wireOp",EDGE,"E0.right");var subQ2=makeQuery(id+"F0.imprint","INTERSECT",VERTEX,{"derivedFrom":[subQ1,subQ0]});Q69=makeQuery(id+"F0.imprint","IMPRINT",FACE,{"disambiguationData":[TD([[makeQuery(id+"F0.imprint","IMPRINT",EDGE,{"disambiguationData":[TD([[subQ2,-1.0]])],"derivedFrom":subQ1}),1.0]])]});}
            var Q70;
            {var subQ0=sQuery(id+"F0.wireOp",EDGE,"fn4HS4Mr-emyM-J1mK-QN5n-hld7hj15i5pK");var subQ1=sQuery(id+"F0.wireOp",EDGE,"E0.right");var subQ2=makeQuery(id+"F0.imprint","INTERSECT",VERTEX,{"derivedFrom":[subQ1,subQ0]});Q70=makeQuery(id+"F0.imprint","IMPRINT",FACE,{"disambiguationData":[TD([[makeQuery(id+"F0.imprint","IMPRINT",EDGE,{"disambiguationData":[TD([[subQ2,-1.0]])],"derivedFrom":subQ1}),1.0]])]});}
            var Q71;
            Q71=makeQuery(id+"F0.imprint","IMPRINT",FACE,{"disambiguationData":[TD([[makeQuery(id+"F0.imprint","IMPRINT",EDGE,{"derivedFrom":sQuery(id+"F0.wireOp",EDGE,"E29.7.0.0")}),1.0]])]});
            var Q72;
            Q72=makeQuery(id+"F0.imprint","IMPRINT",FACE,{"disambiguationData":[TD([[makeQuery(id+"F0.imprint","IMPRINT",EDGE,{"derivedFrom":sQuery(id+"F0.wireOp",EDGE,"E29.6.0.3")}),1.0]])]});
            var Q73;
            {var subQ0=sQuery(id+"F0.wireOp",EDGE,"E53");var subQ1=sQuery(id+"F0.wireOp",EDGE,"E0.right");var subQ2=makeQuery(id+"F0.imprint","INTERSECT",VERTEX,{"derivedFrom":[subQ1,subQ0]});Q73=makeQuery(id+"F0.imprint","IMPRINT",FACE,{"disambiguationData":[TD([[makeQuery(id+"F0.imprint","IMPRINT",EDGE,{"disambiguationData":[TD([[subQ2,-1.0]])],"derivedFrom":subQ1}),1.0]])]});}
            var Q74;
            {var subQ0=sQuery(id+"F0.wireOp",EDGE,"E52");var subQ1=sQuery(id+"F0.wireOp",EDGE,"E0.right");var subQ2=makeQuery(id+"F0.imprint","INTERSECT",VERTEX,{"derivedFrom":[subQ1,subQ0]});Q74=makeQuery(id+"F0.imprint","IMPRINT",FACE,{"disambiguationData":[TD([[makeQuery(id+"F0.imprint","IMPRINT",EDGE,{"disambiguationData":[TD([[subQ2,-1.0]])],"derivedFrom":subQ1}),1.0]])]});}
            var Q75;
            Q75=makeQuery(id+"F0.imprint","IMPRINT",FACE,{"disambiguationData":[TD([[makeQuery(id+"F0.imprint","IMPRINT",EDGE,{"derivedFrom":sQuery(id+"F0.wireOp",EDGE,"E29.6.0.0")}),1.0]])]});
            var Q76;
            {var subQ0=sQuery(id+"F0.wireOp",EDGE,"E51");var subQ1=sQuery(id+"F0.wireOp",EDGE,"E0.right");var subQ2=makeQuery(id+"F0.imprint","INTERSECT",VERTEX,{"derivedFrom":[subQ1,subQ0]});Q76=makeQuery(id+"F0.imprint","IMPRINT",FACE,{"disambiguationData":[TD([[makeQuery(id+"F0.imprint","IMPRINT",EDGE,{"disambiguationData":[TD([[subQ2,-1.0]])],"derivedFrom":subQ1}),1.0]])]});}
            var Q77;
            Q77=makeQuery(id+"F0.imprint","IMPRINT",FACE,{"disambiguationData":[TD([[makeQuery(id+"F0.imprint","IMPRINT",EDGE,{"derivedFrom":sQuery(id+"F0.wireOp",EDGE,"E29.5.0.3")}),1.0]])]});
            var Q78;
            {var subQ0=sQuery(id+"F0.wireOp",EDGE,"E50");var subQ1=sQuery(id+"F0.wireOp",EDGE,"E0.right");var subQ2=makeQuery(id+"F0.imprint","INTERSECT",VERTEX,{"derivedFrom":[subQ1,subQ0]});Q78=makeQuery(id+"F0.imprint","IMPRINT",FACE,{"disambiguationData":[TD([[makeQuery(id+"F0.imprint","IMPRINT",EDGE,{"disambiguationData":[TD([[subQ2,-1.0]])],"derivedFrom":subQ1}),1.0]])]});}
            var Q79;
            Q79=makeQuery(id+"F0.imprint","IMPRINT",FACE,{"disambiguationData":[TD([[makeQuery(id+"F0.imprint","IMPRINT",EDGE,{"derivedFrom":sQuery(id+"F0.wireOp",EDGE,"E29.5.0.0")}),1.0]])]});
            var Q80;
            {var subQ0=sQuery(id+"F0.wireOp",EDGE,"E49");var subQ1=sQuery(id+"F0.wireOp",EDGE,"E0.right");var subQ2=makeQuery(id+"F0.imprint","INTERSECT",VERTEX,{"derivedFrom":[subQ1,subQ0]});Q80=makeQuery(id+"F0.imprint","IMPRINT",FACE,{"disambiguationData":[TD([[makeQuery(id+"F0.imprint","IMPRINT",EDGE,{"disambiguationData":[TD([[subQ2,-1.0]])],"derivedFrom":subQ1}),1.0]])]});}
            var Q81;
            Q81=makeQuery(id+"F0.imprint","IMPRINT",FACE,{"disambiguationData":[TD([[makeQuery(id+"F0.imprint","IMPRINT",EDGE,{"derivedFrom":sQuery(id+"F0.wireOp",EDGE,"E29.4.0.3")}),1.0]])]});
            var Q82;
            {var subQ0=sQuery(id+"F0.wireOp",EDGE,"E48");var subQ1=sQuery(id+"F0.wireOp",EDGE,"E0.right");var subQ2=makeQuery(id+"F0.imprint","INTERSECT",VERTEX,{"derivedFrom":[subQ1,subQ0]});Q82=makeQuery(id+"F0.imprint","IMPRINT",FACE,{"disambiguationData":[TD([[makeQuery(id+"F0.imprint","IMPRINT",EDGE,{"disambiguationData":[TD([[subQ2,-1.0]])],"derivedFrom":subQ1}),1.0]])]});}
            var Q83;
            Q83=makeQuery(id+"F0.imprint","IMPRINT",FACE,{"disambiguationData":[TD([[makeQuery(id+"F0.imprint","IMPRINT",EDGE,{"derivedFrom":sQuery(id+"F0.wireOp",EDGE,"E29.4.0.0")}),1.0]])]});
            var Q84;
            Q84=makeQuery(id+"F0.imprint","IMPRINT",FACE,{"disambiguationData":[TD([[makeQuery(id+"F0.imprint","IMPRINT",EDGE,{"derivedFrom":sQuery(id+"F0.wireOp",EDGE,"E29.3.0.3")}),1.0]])]});
            var Q85;
            {var subQ0=sQuery(id+"F0.wireOp",EDGE,"E41");var subQ1=sQuery(id+"F0.wireOp",EDGE,"E0.right");var subQ2=makeQuery(id+"F0.imprint","INTERSECT",VERTEX,{"derivedFrom":[subQ1,subQ0]});Q85=makeQuery(id+"F0.imprint","IMPRINT",FACE,{"disambiguationData":[TD([[makeQuery(id+"F0.imprint","IMPRINT",EDGE,{"disambiguationData":[TD([[subQ2,-1.0]])],"derivedFrom":subQ1}),1.0]])]});}
            var Q86;
            {var subQ0=sQuery(id+"F0.wireOp",EDGE,"E40");var subQ1=sQuery(id+"F0.wireOp",EDGE,"E0.right");var subQ2=makeQuery(id+"F0.imprint","INTERSECT",VERTEX,{"derivedFrom":[subQ1,subQ0]});Q86=makeQuery(id+"F0.imprint","IMPRINT",FACE,{"disambiguationData":[TD([[makeQuery(id+"F0.imprint","IMPRINT",EDGE,{"disambiguationData":[TD([[subQ2,-1.0]])],"derivedFrom":subQ1}),1.0]])]});}
            var Q87;
            Q87=makeQuery(id+"F0.imprint","IMPRINT",FACE,{"disambiguationData":[TD([[makeQuery(id+"F0.imprint","IMPRINT",EDGE,{"derivedFrom":sQuery(id+"F0.wireOp",EDGE,"E29.3.0.0")}),1.0]])]});
            var Q88;
            Q88=makeQuery(id+"F0.imprint","IMPRINT",FACE,{"disambiguationData":[TD([[makeQuery(id+"F0.imprint","IMPRINT",EDGE,{"derivedFrom":sQuery(id+"F0.wireOp",EDGE,"E29.2.0.3")}),1.0]])]});
            var Q89;
            {var subQ0=sQuery(id+"F0.wireOp",EDGE,"E37");var subQ1=sQuery(id+"F0.wireOp",EDGE,"E0.right");var subQ2=makeQuery(id+"F0.imprint","INTERSECT",VERTEX,{"derivedFrom":[subQ1,subQ0]});Q89=makeQuery(id+"F0.imprint","IMPRINT",FACE,{"disambiguationData":[TD([[makeQuery(id+"F0.imprint","IMPRINT",EDGE,{"disambiguationData":[TD([[subQ2,-1.0]])],"derivedFrom":subQ1}),1.0]])]});}
            var Q90;
            {var subQ0=sQuery(id+"F0.wireOp",EDGE,"E36");var subQ1=sQuery(id+"F0.wireOp",EDGE,"E0.right");var subQ2=makeQuery(id+"F0.imprint","INTERSECT",VERTEX,{"derivedFrom":[subQ1,subQ0]});Q90=makeQuery(id+"F0.imprint","IMPRINT",FACE,{"disambiguationData":[TD([[makeQuery(id+"F0.imprint","IMPRINT",EDGE,{"disambiguationData":[TD([[subQ2,-1.0]])],"derivedFrom":subQ1}),1.0]])]});}
            var Q91;
            Q91=makeQuery(id+"F0.imprint","IMPRINT",FACE,{"disambiguationData":[TD([[makeQuery(id+"F0.imprint","IMPRINT",EDGE,{"derivedFrom":sQuery(id+"F0.wireOp",EDGE,"E29.2.0.0")}),1.0]])]});
            var Q92;
            Q92=makeQuery(id+"F0.imprint","IMPRINT",FACE,{"disambiguationData":[TD([[makeQuery(id+"F0.imprint","IMPRINT",EDGE,{"derivedFrom":sQuery(id+"F0.wireOp",EDGE,"E29.1.0.3")}),1.0]])]});
            var Q93;
            {var subQ0=sQuery(id+"F0.wireOp",EDGE,"E33");var subQ1=sQuery(id+"F0.wireOp",EDGE,"E0.right");var subQ2=makeQuery(id+"F0.imprint","INTERSECT",VERTEX,{"derivedFrom":[subQ1,subQ0]});Q93=makeQuery(id+"F0.imprint","IMPRINT",FACE,{"disambiguationData":[TD([[makeQuery(id+"F0.imprint","IMPRINT",EDGE,{"disambiguationData":[TD([[subQ2,-1.0]])],"derivedFrom":subQ1}),1.0]])]});}
            var Q94;
            {var subQ0=sQuery(id+"F0.wireOp",EDGE,"E32");var subQ1=sQuery(id+"F0.wireOp",EDGE,"E0.right");var subQ2=makeQuery(id+"F0.imprint","INTERSECT",VERTEX,{"derivedFrom":[subQ1,subQ0]});Q94=makeQuery(id+"F0.imprint","IMPRINT",FACE,{"disambiguationData":[TD([[makeQuery(id+"F0.imprint","IMPRINT",EDGE,{"disambiguationData":[TD([[subQ2,-1.0]])],"derivedFrom":subQ1}),1.0]])]});}
            var Q95;
            Q95=makeQuery(id+"F0.imprint","IMPRINT",FACE,{"disambiguationData":[TD([[makeQuery(id+"F0.imprint","IMPRINT",EDGE,{"derivedFrom":sQuery(id+"F0.wireOp",EDGE,"E29.1.0.0")}),1.0]])]});
            var Q96;
            {var subQ5=sQuery(id+"F0.wireOp",EDGE,"E24");Q96=makeQuery(id+"F0.imprint","IMPRINT",FACE,{"disambiguationData":[TD([[makeQuery(id+"F0.imprint","IMPRINT",EDGE,{"derivedFrom":subQ5}),1.0]])]});}
            var Q97;
            {var subQ0=sQuery(id+"F0.wireOp",EDGE,"E28");Q97=makeQuery(id+"F0.imprint","IMPRINT",FACE,{"disambiguationData":[TD([[makeQuery(id+"F0.imprint","IMPRINT",EDGE,{"derivedFrom":subQ0}),1.0]])]});}
            var Q98;
            {var subQ3=sQuery(id+"F0.wireOp",EDGE,"E23");Q98=makeQuery(id+"F0.imprint","IMPRINT",FACE,{"disambiguationData":[TD([[makeQuery(id+"F0.imprint","IMPRINT",EDGE,{"derivedFrom":subQ3}),1.0]])]});}
            var Q99;
            {var subQ1=sQuery(id+"F0.wireOp",EDGE,"E19");Q99=makeQuery(id+"F0.imprint","IMPRINT",FACE,{"disambiguationData":[TD([[makeQuery(id+"F0.imprint","IMPRINT",EDGE,{"derivedFrom":subQ1}),1.0]])]});}
            var Q100;
            Q100=makeQuery(id+"F0.imprint","IMPRINT",FACE,{"disambiguationData":[TD([[makeQuery(id+"F0.imprint","IMPRINT",EDGE,{"derivedFrom":sQuery(id+"F0.wireOp",EDGE,"zQGFcMV2-mCyC-DOFT-t9AW-xuzp7DauXhaW")}),-1.0]])]});
            extrude(context, id + "F1", {"entities" : qUnion([Q0, Q1, Q2, Q3, Q4, Q5, Q6, Q7, Q8, Q9, Q10, Q11, Q12, Q13, Q14, Q15, Q16, Q17, Q18, Q19, Q20, Q21, Q22, Q23, Q24, Q25, Q26, Q27, Q28, Q29, Q30, Q31, Q32, Q33, Q34, Q35, Q36, Q37, Q38, Q39, Q40, Q41, Q42, Q43, Q44, Q45, Q46, Q47, Q48, Q49, Q50, Q51, Q52, Q53, Q54, Q55, Q56, Q57, Q58, Q59, Q60, Q61, Q62, Q63, Q64, Q65, Q66, Q67, Q68, Q69, Q70, Q71, Q72, Q73, Q74, Q75, Q76, Q77, Q78, Q79, Q80, Q81, Q82, Q83, Q84, Q85, Q86, Q87, Q88, Q89, Q90, Q91, Q92, Q93, Q94, Q95, Q96, Q97, Q98, Q99, Q100]), "oppositeDirection" : true, "depth" : 6.35 * mm});
        }
        {
            var Q0;
            Q0=makeQuery(id+"F0.imprint","IMPRINT",FACE,{"disambiguationData":[TD([[makeQuery(id+"F0.imprint","IMPRINT",EDGE,{"derivedFrom":sQuery(id+"F0.wireOp",EDGE,"E82.MirrorCS")}),-1.0]])]});
            var Q1;
            {var subQ6=sQuery(id+"F0.wireOp",EDGE,"E87.MirrorCS");Q1=makeQuery(id+"F0.imprint","IMPRINT",FACE,{"disambiguationData":[TD([[makeQuery(id+"F0.imprint","IMPRINT",EDGE,{"derivedFrom":subQ6}),1.0]])]});}
            var Q2;
            {var subQ0=sQuery(id+"F0.wireOp",EDGE,"E10.top");Q2=makeQuery(id+"F0.imprint","IMPRINT",FACE,{"disambiguationData":[TD([[makeQuery(id+"F0.imprint","IMPRINT",EDGE,{"derivedFrom":subQ0}),1.0]])]});}
            var Q3;
            {var subQ8=sQuery(id+"F0.wireOp",EDGE,"E75.MirrorCS");Q3=makeQuery(id+"F0.imprint","IMPRINT",FACE,{"disambiguationData":[TD([[makeQuery(id+"F0.imprint","IMPRINT",EDGE,{"derivedFrom":subQ8}),1.0]])]});}
            var Q4;
            {var subQ6=sQuery(id+"F0.wireOp",EDGE,"E69.MirrorCS");Q4=makeQuery(id+"F0.imprint","IMPRINT",FACE,{"disambiguationData":[TD([[makeQuery(id+"F0.imprint","IMPRINT",EDGE,{"derivedFrom":subQ6}),1.0]])]});}
            var Q5;
            {var subQ7=sQuery(id+"F0.wireOp",EDGE,"E63.MirrorCS");Q5=makeQuery(id+"F0.imprint","IMPRINT",FACE,{"disambiguationData":[TD([[makeQuery(id+"F0.imprint","IMPRINT",EDGE,{"derivedFrom":subQ7}),1.0]])]});}
            var Q6;
            {var subQ7=sQuery(id+"F0.wireOp",EDGE,"E57.MirrorCS");Q6=makeQuery(id+"F0.imprint","IMPRINT",FACE,{"disambiguationData":[TD([[makeQuery(id+"F0.imprint","IMPRINT",EDGE,{"derivedFrom":subQ7}),1.0]])]});}
            var Q7;
            {var subQ7=sQuery(id+"F0.wireOp",EDGE,"859455d8-9afb-47e5-a04d-dad7f7b3347415.MirrorCS");Q7=makeQuery(id+"F0.imprint","IMPRINT",FACE,{"disambiguationData":[TD([[makeQuery(id+"F0.imprint","IMPRINT",EDGE,{"derivedFrom":subQ7}),1.0]])]});}
            var Q8;
            {var subQ3=sQuery(id+"F0.wireOp",EDGE,"859455d8-9afb-47e5-a04d-dad7f7b334749.MirrorCS");Q8=makeQuery(id+"F0.imprint","IMPRINT",FACE,{"disambiguationData":[TD([[makeQuery(id+"F0.imprint","IMPRINT",EDGE,{"derivedFrom":subQ3}),1.0]])]});}
            var Q9;
            {var subQ9=sQuery(id+"F0.wireOp",EDGE,"859455d8-9afb-47e5-a04d-dad7f7b334743.MirrorCS");Q9=makeQuery(id+"F0.imprint","IMPRINT",FACE,{"disambiguationData":[TD([[makeQuery(id+"F0.imprint","IMPRINT",EDGE,{"derivedFrom":subQ9}),1.0]])]});}
            var Q10;
            {var subQ4=sQuery(id+"F0.wireOp",EDGE,"859455d8-9afb-47e5-a04d-dad7f7b334740.MirrorCS");Q10=makeQuery(id+"F0.imprint","IMPRINT",FACE,{"disambiguationData":[TD([[makeQuery(id+"F0.imprint","IMPRINT",EDGE,{"derivedFrom":subQ4}),-1.0]])]});}
            var Q11;
            {var subQ0=sQuery(id+"F0.wireOp",EDGE,"E14.MirrorCS");var subQ1=sQuery(id+"F0.wireOp",EDGE,"E5.top");var subQ2=makeQuery(id+"F0.imprint","INTERSECT",VERTEX,{"derivedFrom":[subQ1,subQ0]});Q11=makeQuery(id+"F0.imprint","IMPRINT",FACE,{"disambiguationData":[TD([[makeQuery(id+"F0.imprint","IMPRINT",EDGE,{"disambiguationData":[TD([[subQ2,-1.0]])],"derivedFrom":subQ1}),-1.0]])]});}
            var Q12;
            {var subQ0=sQuery(id+"F0.wireOp",EDGE,"E14.MirrorCS");var subQ1=sQuery(id+"F0.wireOp",EDGE,"E5.top");var subQ2=makeQuery(id+"F0.imprint","INTERSECT",VERTEX,{"derivedFrom":[subQ1,subQ0]});Q12=makeQuery(id+"F0.imprint","IMPRINT",FACE,{"disambiguationData":[TD([[makeQuery(id+"F0.imprint","IMPRINT",EDGE,{"disambiguationData":[TD([[subQ2,1.0]])],"derivedFrom":subQ1}),-1.0]])]});}
            var Q13;
            {var subQ0=sQuery(id+"F0.wireOp",EDGE,"7ab7f921-5da6-4109-8e3c-2e87eee36be50.MirrorCS");var subQ1=sQuery(id+"F0.wireOp",EDGE,"E5.top");var subQ2=makeQuery(id+"F0.imprint","INTERSECT",VERTEX,{"derivedFrom":[subQ1,subQ0]});Q13=makeQuery(id+"F0.imprint","IMPRINT",FACE,{"disambiguationData":[TD([[makeQuery(id+"F0.imprint","IMPRINT",EDGE,{"disambiguationData":[TD([[subQ2,1.0]])],"derivedFrom":subQ1}),-1.0]])]});}
            var Q14;
            Q14=makeQuery(id+"F0.imprint","IMPRINT",FACE,{"disambiguationData":[TD([[makeQuery(id+"F0.imprint","IMPRINT",EDGE,{"derivedFrom":sQuery(id+"F0.wireOp",EDGE,"E29.9.0.3")}),1.0]])]});
            var Q15;
            Q15=makeQuery(id+"F0.imprint","IMPRINT",FACE,{"disambiguationData":[TD([[makeQuery(id+"F0.imprint","IMPRINT",EDGE,{"derivedFrom":sQuery(id+"F0.wireOp",EDGE,"E29.8.0.3")}),1.0]])]});
            var Q16;
            Q16=makeQuery(id+"F0.imprint","IMPRINT",FACE,{"disambiguationData":[TD([[makeQuery(id+"F0.imprint","IMPRINT",EDGE,{"derivedFrom":sQuery(id+"F0.wireOp",EDGE,"E29.7.0.3")}),1.0]])]});
            var Q17;
            Q17=makeQuery(id+"F0.imprint","IMPRINT",FACE,{"disambiguationData":[TD([[makeQuery(id+"F0.imprint","IMPRINT",EDGE,{"derivedFrom":sQuery(id+"F0.wireOp",EDGE,"E29.6.0.3")}),1.0]])]});
            var Q18;
            Q18=makeQuery(id+"F0.imprint","IMPRINT",FACE,{"disambiguationData":[TD([[makeQuery(id+"F0.imprint","IMPRINT",EDGE,{"derivedFrom":sQuery(id+"F0.wireOp",EDGE,"E29.5.0.3")}),1.0]])]});
            var Q19;
            Q19=makeQuery(id+"F0.imprint","IMPRINT",FACE,{"disambiguationData":[TD([[makeQuery(id+"F0.imprint","IMPRINT",EDGE,{"derivedFrom":sQuery(id+"F0.wireOp",EDGE,"E29.4.0.3")}),1.0]])]});
            var Q20;
            Q20=makeQuery(id+"F0.imprint","IMPRINT",FACE,{"disambiguationData":[TD([[makeQuery(id+"F0.imprint","IMPRINT",EDGE,{"derivedFrom":sQuery(id+"F0.wireOp",EDGE,"E29.3.0.3")}),1.0]])]});
            var Q21;
            Q21=makeQuery(id+"F0.imprint","IMPRINT",FACE,{"disambiguationData":[TD([[makeQuery(id+"F0.imprint","IMPRINT",EDGE,{"derivedFrom":sQuery(id+"F0.wireOp",EDGE,"E29.2.0.3")}),1.0]])]});
            var Q22;
            Q22=makeQuery(id+"F0.imprint","IMPRINT",FACE,{"disambiguationData":[TD([[makeQuery(id+"F0.imprint","IMPRINT",EDGE,{"derivedFrom":sQuery(id+"F0.wireOp",EDGE,"E29.1.0.3")}),1.0]])]});
            var Q23;
            {var subQ5=sQuery(id+"F0.wireOp",EDGE,"E24");Q23=makeQuery(id+"F0.imprint","IMPRINT",FACE,{"disambiguationData":[TD([[makeQuery(id+"F0.imprint","IMPRINT",EDGE,{"derivedFrom":subQ5}),1.0]])]});}
            var Q24;
            {var subQ0=sQuery(id+"F0.wireOp",EDGE,"E19");Q24=makeQuery(id+"F0.imprint","IMPRINT",FACE,{"disambiguationData":[TD([[makeQuery(id+"F0.imprint","IMPRINT",EDGE,{"derivedFrom":subQ0}),-1.0]])]});}
            var Q25;
            {var subQ1=sQuery(id+"F0.wireOp",EDGE,"E5.bottom");var subQ3=sQuery(id+"F0.wireOp",EDGE,"7fccda47-ab33-4617-952b-09ef6f2d93c20.MirrorCS");var subQ4=makeQuery(id+"F0.imprint","INTERSECT",VERTEX,{"derivedFrom":[subQ1,subQ3]});Q25=makeQuery(id+"F0.imprint","IMPRINT",FACE,{"disambiguationData":[TD([[makeQuery(id+"F0.imprint","IMPRINT",EDGE,{"disambiguationData":[TD([[subQ4,1.0]])],"derivedFrom":subQ3}),1.0]])]});}
            var Q26;
            Q26=makeQuery(id+"F0.imprint","IMPRINT",FACE,{"disambiguationData":[TD([[makeQuery(id+"F0.imprint","IMPRINT",EDGE,{"derivedFrom":sQuery(id+"F0.wireOp",EDGE,"E83.MirrorCS")}),1.0]])]});
            var Q27;
            {var subQ0=sQuery(id+"F0.wireOp",EDGE,"7fccda47-ab33-4617-952b-09ef6f2d93c20.MirrorCS");var subQ1=sQuery(id+"F0.wireOp",EDGE,"E5.bottom");var subQ2=makeQuery(id+"F0.imprint","INTERSECT",VERTEX,{"derivedFrom":[subQ1,subQ0]});Q27=makeQuery(id+"F0.imprint","IMPRINT",FACE,{"disambiguationData":[TD([[makeQuery(id+"F0.imprint","IMPRINT",EDGE,{"disambiguationData":[TD([[subQ2,1.0]])],"derivedFrom":subQ1}),1.0]])]});}
            extrude(context, id + "F2", {"entities" : qUnion([Q0, Q1, Q2, Q3, Q4, Q5, Q6, Q7, Q8, Q9, Q10, Q11, Q12, Q13, Q14, Q15, Q16, Q17, Q18, Q19, Q20, Q21, Q22, Q23, Q24, Q25, Q26, Q27]), "operationType" : NewBodyOperationType.ADD, "depth" : 38.1 * mm});
        }
        {
            var Q0;
            {var subQ0=sQuery(id+"F0.wireOp",EDGE,"E28");Q0=makeQuery(id+"F0.imprint","IMPRINT",FACE,{"disambiguationData":[TD([[makeQuery(id+"F0.imprint","IMPRINT",EDGE,{"derivedFrom":subQ0}),1.0]])]});}
            var Q1;
            {var subQ0=sQuery(id+"F0.wireOp",EDGE,"E33");var subQ1=sQuery(id+"F0.wireOp",EDGE,"E0.right");var subQ2=makeQuery(id+"F0.imprint","INTERSECT",VERTEX,{"derivedFrom":[subQ1,subQ0]});Q1=makeQuery(id+"F0.imprint","IMPRINT",FACE,{"disambiguationData":[TD([[makeQuery(id+"F0.imprint","IMPRINT",EDGE,{"disambiguationData":[TD([[subQ2,-1.0]])],"derivedFrom":subQ1}),1.0]])]});}
            var Q2;
            {var subQ0=sQuery(id+"F0.wireOp",EDGE,"E37");var subQ1=sQuery(id+"F0.wireOp",EDGE,"E0.right");var subQ2=makeQuery(id+"F0.imprint","INTERSECT",VERTEX,{"derivedFrom":[subQ1,subQ0]});Q2=makeQuery(id+"F0.imprint","IMPRINT",FACE,{"disambiguationData":[TD([[makeQuery(id+"F0.imprint","IMPRINT",EDGE,{"disambiguationData":[TD([[subQ2,-1.0]])],"derivedFrom":subQ1}),1.0]])]});}
            var Q3;
            {var subQ0=sQuery(id+"F0.wireOp",EDGE,"E41");var subQ1=sQuery(id+"F0.wireOp",EDGE,"E0.right");var subQ2=makeQuery(id+"F0.imprint","INTERSECT",VERTEX,{"derivedFrom":[subQ1,subQ0]});Q3=makeQuery(id+"F0.imprint","IMPRINT",FACE,{"disambiguationData":[TD([[makeQuery(id+"F0.imprint","IMPRINT",EDGE,{"disambiguationData":[TD([[subQ2,-1.0]])],"derivedFrom":subQ1}),1.0]])]});}
            var Q4;
            {var subQ0=sQuery(id+"F0.wireOp",EDGE,"E49");var subQ1=sQuery(id+"F0.wireOp",EDGE,"E0.right");var subQ2=makeQuery(id+"F0.imprint","INTERSECT",VERTEX,{"derivedFrom":[subQ1,subQ0]});Q4=makeQuery(id+"F0.imprint","IMPRINT",FACE,{"disambiguationData":[TD([[makeQuery(id+"F0.imprint","IMPRINT",EDGE,{"disambiguationData":[TD([[subQ2,-1.0]])],"derivedFrom":subQ1}),1.0]])]});}
            var Q5;
            {var subQ0=sQuery(id+"F0.wireOp",EDGE,"E51");var subQ1=sQuery(id+"F0.wireOp",EDGE,"E0.right");var subQ2=makeQuery(id+"F0.imprint","INTERSECT",VERTEX,{"derivedFrom":[subQ1,subQ0]});Q5=makeQuery(id+"F0.imprint","IMPRINT",FACE,{"disambiguationData":[TD([[makeQuery(id+"F0.imprint","IMPRINT",EDGE,{"disambiguationData":[TD([[subQ2,-1.0]])],"derivedFrom":subQ1}),1.0]])]});}
            var Q6;
            {var subQ5=sQuery(id+"F0.wireOp",EDGE,"E4.filletArc");Q6=makeQuery(id+"F0.imprint","IMPRINT",FACE,{"disambiguationData":[TD([[makeQuery(id+"F0.imprint","IMPRINT",EDGE,{"derivedFrom":subQ5}),1.0]])]});}
            var Q7;
            {var subQ9=sQuery(id+"F0.wireOp",EDGE,"E3.filletArc");Q7=makeQuery(id+"F0.imprint","IMPRINT",FACE,{"disambiguationData":[TD([[makeQuery(id+"F0.imprint","IMPRINT",EDGE,{"derivedFrom":subQ9}),1.0]])]});}
            var Q8;
            {var subQ0=sQuery(id+"F0.wireOp",EDGE,"E14.MirrorCS");var subQ5=sQuery(id+"F0.wireOp",EDGE,"E131");var subQ6=makeQuery(id+"F0.imprint","INTERSECT",VERTEX,{"derivedFrom":[subQ0,subQ5]});Q8=makeQuery(id+"F0.imprint","IMPRINT",FACE,{"disambiguationData":[TD([[makeQuery(id+"F0.imprint","IMPRINT",EDGE,{"disambiguationData":[TD([[subQ6,-1.0]])],"derivedFrom":subQ5}),-1.0]])]});}
            var Q9;
            {var subQ5=sQuery(id+"F0.wireOp",EDGE,"E2.filletArc");Q9=makeQuery(id+"F0.imprint","IMPRINT",FACE,{"disambiguationData":[TD([[makeQuery(id+"F0.imprint","IMPRINT",EDGE,{"derivedFrom":subQ5}),1.0]])]});}
            var Q10;
            {var subQ0=sQuery(id+"F0.wireOp",EDGE,"E99");Q10=makeQuery(id+"F0.imprint","IMPRINT",FACE,{"disambiguationData":[TD([[makeQuery(id+"F0.imprint","IMPRINT",EDGE,{"derivedFrom":subQ0}),-1.0]])]});}
            var Q11;
            {var subQ0=sQuery(id+"F0.wireOp",EDGE,"E101");var subQ1=sQuery(id+"F0.wireOp",EDGE,"E0.left");var subQ2=makeQuery(id+"F0.imprint","INTERSECT",VERTEX,{"derivedFrom":[subQ1,subQ0]});Q11=makeQuery(id+"F0.imprint","IMPRINT",FACE,{"disambiguationData":[TD([[makeQuery(id+"F0.imprint","IMPRINT",EDGE,{"disambiguationData":[TD([[subQ2,-1.0]])],"derivedFrom":subQ1}),-1.0]])]});}
            var Q12;
            {var subQ0=sQuery(id+"F0.wireOp",EDGE,"E105");var subQ1=sQuery(id+"F0.wireOp",EDGE,"E0.left");var subQ2=makeQuery(id+"F0.imprint","INTERSECT",VERTEX,{"derivedFrom":[subQ1,subQ0]});Q12=makeQuery(id+"F0.imprint","IMPRINT",FACE,{"disambiguationData":[TD([[makeQuery(id+"F0.imprint","IMPRINT",EDGE,{"disambiguationData":[TD([[subQ2,-1.0]])],"derivedFrom":subQ1}),-1.0]])]});}
            var Q13;
            {var subQ0=sQuery(id+"F0.wireOp",EDGE,"E109");var subQ1=sQuery(id+"F0.wireOp",EDGE,"E0.left");var subQ2=makeQuery(id+"F0.imprint","INTERSECT",VERTEX,{"derivedFrom":[subQ1,subQ0]});Q13=makeQuery(id+"F0.imprint","IMPRINT",FACE,{"disambiguationData":[TD([[makeQuery(id+"F0.imprint","IMPRINT",EDGE,{"disambiguationData":[TD([[subQ2,-1.0]])],"derivedFrom":subQ1}),-1.0]])]});}
            var Q14;
            {var subQ0=sQuery(id+"F0.wireOp",EDGE,"E113");var subQ1=sQuery(id+"F0.wireOp",EDGE,"E0.left");var subQ2=makeQuery(id+"F0.imprint","INTERSECT",VERTEX,{"derivedFrom":[subQ1,subQ0]});Q14=makeQuery(id+"F0.imprint","IMPRINT",FACE,{"disambiguationData":[TD([[makeQuery(id+"F0.imprint","IMPRINT",EDGE,{"disambiguationData":[TD([[subQ2,-1.0]])],"derivedFrom":subQ1}),-1.0]])]});}
            var Q15;
            {var subQ0=sQuery(id+"F0.wireOp",EDGE,"E117");var subQ1=sQuery(id+"F0.wireOp",EDGE,"E0.left");var subQ2=makeQuery(id+"F0.imprint","INTERSECT",VERTEX,{"derivedFrom":[subQ1,subQ0]});Q15=makeQuery(id+"F0.imprint","IMPRINT",FACE,{"disambiguationData":[TD([[makeQuery(id+"F0.imprint","IMPRINT",EDGE,{"disambiguationData":[TD([[subQ2,-1.0]])],"derivedFrom":subQ1}),-1.0]])]});}
            var Q16;
            {var subQ0=sQuery(id+"F0.wireOp",EDGE,"E1.filletArc");Q16=makeQuery(id+"F0.imprint","IMPRINT",FACE,{"disambiguationData":[TD([[makeQuery(id+"F0.imprint","IMPRINT",EDGE,{"derivedFrom":subQ0}),1.0]])]});}
            var Q17;
            {var subQ0=sQuery(id+"F0.wireOp",EDGE,"E10.bottom");Q17=makeQuery(id+"F0.imprint","IMPRINT",FACE,{"disambiguationData":[TD([[makeQuery(id+"F0.imprint","IMPRINT",EDGE,{"derivedFrom":subQ0}),-1.0]])]});}
            var Q18;
            {var subQ0=sQuery(id+"F0.wireOp",EDGE,"7fccda47-ab33-4617-952b-09ef6f2d93c20.MirrorCS");var subQ5=sQuery(id+"F0.wireOp",EDGE,"E126");var subQ6=makeQuery(id+"F0.imprint","INTERSECT",VERTEX,{"derivedFrom":[subQ0,subQ5]});Q18=makeQuery(id+"F0.imprint","IMPRINT",FACE,{"disambiguationData":[TD([[makeQuery(id+"F0.imprint","IMPRINT",EDGE,{"disambiguationData":[TD([[subQ6,1.0]])],"derivedFrom":subQ5}),1.0]])]});}
            var Q19;
            {var subQ0=sQuery(id+"F0.wireOp",EDGE,"E10.left");var subQ5=sQuery(id+"F0.wireOp",EDGE,"E126");var subQ6=makeQuery(id+"F0.imprint","INTERSECT",VERTEX,{"derivedFrom":[subQ0,subQ5]});Q19=makeQuery(id+"F0.imprint","IMPRINT",FACE,{"disambiguationData":[TD([[makeQuery(id+"F0.imprint","IMPRINT",EDGE,{"disambiguationData":[TD([[subQ6,1.0]])],"derivedFrom":subQ5}),1.0]])]});}
            var Q20;
            {var subQ0=sQuery(id+"F0.wireOp",EDGE,"E14.MirrorCS");var subQ5=sQuery(id+"F0.wireOp",EDGE,"E131");var subQ6=makeQuery(id+"F0.imprint","INTERSECT",VERTEX,{"derivedFrom":[subQ0,subQ5]});Q20=makeQuery(id+"F0.imprint","IMPRINT",FACE,{"disambiguationData":[TD([[makeQuery(id+"F0.imprint","IMPRINT",EDGE,{"disambiguationData":[TD([[subQ6,1.0]])],"derivedFrom":subQ5}),-1.0]])]});}
            var Q21;
            {var subQ0=sQuery(id+"F0.wireOp",EDGE,"7ab7f921-5da6-4109-8e3c-2e87eee36be50.MirrorCS");var subQ5=sQuery(id+"F0.wireOp",EDGE,"E131");var subQ6=makeQuery(id+"F0.imprint","INTERSECT",VERTEX,{"derivedFrom":[subQ0,subQ5]});Q21=makeQuery(id+"F0.imprint","IMPRINT",FACE,{"disambiguationData":[TD([[makeQuery(id+"F0.imprint","IMPRINT",EDGE,{"disambiguationData":[TD([[subQ6,1.0]])],"derivedFrom":subQ5}),-1.0]])]});}
            extrude(context, id + "F3", {"entities" : qUnion([Q0, Q1, Q2, Q3, Q4, Q5, Q6, Q7, Q8, Q9, Q10, Q11, Q12, Q13, Q14, Q15, Q16, Q17, Q18, Q19, Q20, Q21]), "operationType" : NewBodyOperationType.ADD, "depth" : 31.75 * mm});
        }
        {
            var Q0;
            Q0=makeQuery(id+"F0.imprint","IMPRINT",FACE,{"disambiguationData":[TD([[makeQuery(id+"F0.imprint","IMPRINT",EDGE,{"derivedFrom":sQuery(id+"F0.wireOp",EDGE,"E132")}),1.0]])]});
            var Q1;
            Q1=makeQuery(id+"F0.imprint","IMPRINT",FACE,{"disambiguationData":[TD([[makeQuery(id+"F0.imprint","IMPRINT",EDGE,{"derivedFrom":sQuery(id+"F0.wireOp",EDGE,"E132")}),-1.0]])]});
            var Q2;
            Q2=makeQuery(id+"F0.imprint","IMPRINT",FACE,{"disambiguationData":[TD([[makeQuery(id+"F0.imprint","IMPRINT",EDGE,{"derivedFrom":sQuery(id+"F0.wireOp",EDGE,"E134")}),1.0]])]});
            var Q3;
            Q3=makeQuery(id+"F0.imprint","IMPRINT",FACE,{"disambiguationData":[TD([[makeQuery(id+"F0.imprint","IMPRINT",EDGE,{"derivedFrom":sQuery(id+"F0.wireOp",EDGE,"E134")}),-1.0]])]});
            var Q4;
            Q4=makeQuery(id+"F0.imprint","IMPRINT",FACE,{"disambiguationData":[TD([[makeQuery(id+"F0.imprint","IMPRINT",EDGE,{"derivedFrom":sQuery(id+"F0.wireOp",EDGE,"E138")}),-1.0]])]});
            var Q5;
            Q5=makeQuery(id+"F0.imprint","IMPRINT",FACE,{"disambiguationData":[TD([[makeQuery(id+"F0.imprint","IMPRINT",EDGE,{"derivedFrom":sQuery(id+"F0.wireOp",EDGE,"E138")}),1.0]])]});
            var Q6;
            Q6=makeQuery(id+"F0.imprint","IMPRINT",FACE,{"disambiguationData":[TD([[makeQuery(id+"F0.imprint","IMPRINT",EDGE,{"derivedFrom":sQuery(id+"F0.wireOp",EDGE,"E136")}),-1.0]])]});
            var Q7;
            Q7=makeQuery(id+"F0.imprint","IMPRINT",FACE,{"disambiguationData":[TD([[makeQuery(id+"F0.imprint","IMPRINT",EDGE,{"derivedFrom":sQuery(id+"F0.wireOp",EDGE,"E136")}),1.0]])]});
            var Q8;
            {var subQ13=sQuery(id+"F0.wireOp",EDGE,"E10.top");Q8=makeQuery(id+"F0.imprint","IMPRINT",FACE,{"disambiguationData":[TD([[makeQuery(id+"F0.imprint","IMPRINT",EDGE,{"derivedFrom":subQ13}),-1.0]])]});}
            var Q9;
            Q9=makeQuery(id+"F3.opExtrude","CAP_FACE",FACE,{"disambiguationData":[OSD([sQuery(id+"F0.wireOp",EDGE,"E0.top"),sQuery(id+"F0.wireOp",EDGE,"E0.left"),sQuery(id+"F0.wireOp",EDGE,"E0.right"),sQuery(id+"F0.wireOp",EDGE,"E2.filletArc"),sQuery(id+"F0.wireOp",EDGE,"E3.filletArc"),sQuery(id+"F0.wireOp",EDGE,"E53"),sQuery(id+"F0.wireOp",EDGE,"E121"),sQuery(id+"F0.wireOp",EDGE,"E124"),sQuery(id+"F0.wireOp",EDGE,"E125"),sQuery(id+"F0.wireOp",EDGE,"E129"),sQuery(id+"F0.wireOp",EDGE,"E130"),sQuery(id+"F0.wireOp",EDGE,"E131")])],"isStart":false});
            var Q10;
            {var subQ1=sQuery(id+"F0.wireOp",EDGE,"E54.MirrorCS");Q10=makeQuery(id+"F0.imprint","IMPRINT",FACE,{"disambiguationData":[TD([[makeQuery(id+"F0.imprint","IMPRINT",EDGE,{"derivedFrom":subQ1}),-1.0]])]});}
            extrude(context, id + "F4", {"entities" : qUnion([Q0, Q1, Q2, Q3, Q4, Q5, Q6, Q7, Q8, Q9, Q10]), "operationType" : NewBodyOperationType.ADD, "oppositeDirection" : true, "depth" : 6.35 * mm});
        }
        {
            var Q0;
            Q0=makeQuery(id+"F0.imprint","IMPRINT",FACE,{"disambiguationData":[TD([[makeQuery(id+"F0.imprint","IMPRINT",EDGE,{"derivedFrom":sQuery(id+"F0.wireOp",EDGE,"E132")}),-1.0]])]});
            var Q1;
            Q1=makeQuery(id+"F0.imprint","IMPRINT",FACE,{"disambiguationData":[TD([[makeQuery(id+"F0.imprint","IMPRINT",EDGE,{"derivedFrom":sQuery(id+"F0.wireOp",EDGE,"E134")}),-1.0]])]});
            var Q2;
            Q2=makeQuery(id+"F0.imprint","IMPRINT",FACE,{"disambiguationData":[TD([[makeQuery(id+"F0.imprint","IMPRINT",EDGE,{"derivedFrom":sQuery(id+"F0.wireOp",EDGE,"E138")}),-1.0]])]});
            var Q3;
            Q3=makeQuery(id+"F0.imprint","IMPRINT",FACE,{"disambiguationData":[TD([[makeQuery(id+"F0.imprint","IMPRINT",EDGE,{"derivedFrom":sQuery(id+"F0.wireOp",EDGE,"E136")}),-1.0]])]});
            extrude(context, id + "F5", {"entities" : qUnion([Q0, Q1, Q2, Q3]), "operationType" : NewBodyOperationType.ADD, "depth" : 3.17 * mm});
        }
        {
            var Q0;
            {var subQ0=sQuery(id+"F0.wireOp",EDGE,"E10.top");var subQ1=sQuery(id+"F0.wireOp",EDGE,"E5.bottom");Q0=makeQuery(id+"F2.boolean.opBoolean","MERGE",FACE,{"derivedFrom":[makeQuery(id+"F1.opExtrude","SWEPT_FACE",FACE,{"disambiguationData":[OSD([subQ1,subQ0])]}),makeQuery(id+"F2.opExtrude","SWEPT_FACE",FACE,{"disambiguationData":[OSD([subQ1,subQ0])]})]});}
            var sketch = newSketch(context, id + "F6", { "sketchPlane" : qUnion([Q0])});
            skLineSegment(sketch, "E140.bottom", {"start": v(-43.1, 4.73) * mm, "end": v(-36, 4.73) * mm});
            skLineSegment(sketch, "E140.top", {"start": v(-43.1, 19.24) * mm, "end": v(-36, 19.24) * mm});
            skLineSegment(sketch, "E140.left", {"start": v(-43.1, 4.73) * mm, "end": v(-43.1, 19.24) * mm});
            skLineSegment(sketch, "E140.right", {"start": v(-36, 4.73) * mm, "end": v(-36, 19.24) * mm});
            skLineSegment(sketch, "E141.bottom", {"start": v(-32.16, 6.66) * mm, "end": v(-25.25, 6.66) * mm});
            skLineSegment(sketch, "E141.top", {"start": v(-32.16, 8.79) * mm, "end": v(-25.25, 8.79) * mm});
            skLineSegment(sketch, "E141.left", {"start": v(-32.16, 6.66) * mm, "end": v(-32.16, 8.79) * mm});
            skLineSegment(sketch, "E141.right", {"start": v(-25.25, 6.66) * mm, "end": v(-25.25, 8.79) * mm});
            skLineSegment(sketch, "E142.bottom", {"start": v(-17.98, 18.46) * mm, "end": v(-1.59, 18.46) * mm});
            skLineSegment(sketch, "E142.top", {"start": v(-17.98, 5.07) * mm, "end": v(-1.59, 5.07) * mm});
            skLineSegment(sketch, "E142.left", {"start": v(-17.98, 18.46) * mm, "end": v(-17.98, 5.07) * mm});
            skLineSegment(sketch, "E142.right", {"start": v(-1.59, 18.46) * mm, "end": v(-1.59, 5.07) * mm});
            skLineSegment(sketch, "E143.bottom", {"start": v(-42.11, 18.25) * mm, "end": v(-36.98, 18.25) * mm});
            skLineSegment(sketch, "E143.top", {"start": v(-42.11, 5.73) * mm, "end": v(-36.98, 5.73) * mm});
            skLineSegment(sketch, "E143.left", {"start": v(-42.11, 18.25) * mm, "end": v(-42.11, 5.73) * mm});
            skLineSegment(sketch, "E143.right", {"start": v(-36.98, 18.25) * mm, "end": v(-36.98, 5.73) * mm});
            skLineSegment(sketch, "E144.bottom", {"start": v(-15.8, 5.07) * mm, "end": v(-3.78, 5.07) * mm});
            skLineSegment(sketch, "E144.top", {"start": v(-15.8, 15.76) * mm, "end": v(-3.78, 15.76) * mm});
            skLineSegment(sketch, "E144.left", {"start": v(-15.8, 5.07) * mm, "end": v(-15.8, 15.76) * mm});
            skLineSegment(sketch, "E144.right", {"start": v(-3.78, 5.07) * mm, "end": v(-3.78, 15.76) * mm});
            skLineSegment(sketch, "E145.bottom", {"start": v(-23.62, 10.77) * mm, "end": v(-33.78, 10.77) * mm});
            skLineSegment(sketch, "E145.top", {"start": v(-23.62, 4.67) * mm, "end": v(-33.78, 4.67) * mm});
            skLineSegment(sketch, "E145.left", {"start": v(-23.62, 10.77) * mm, "end": v(-23.62, 4.67) * mm});
            skLineSegment(sketch, "E145.right", {"start": v(-33.78, 10.77) * mm, "end": v(-33.78, 4.67) * mm});
            skPoint(sketch, "E145.middle", {"position": v(-28.7, 7.72) * mm});
            skPoint(sketch, "E145.middle.positionSnap0", {"position": v(-25.25, 7.72) * mm});
            skPoint(sketch, "E145.middle.positionSnap1", {"position": v(-28.7, 8.79) * mm});
            skPoint(sketch, "E145.centerSnap0", {"position": v(-25.25, 7.72) * mm});
            skPoint(sketch, "E145.centerSnap1", {"position": v(-28.7, 8.79) * mm});
            skSolve(sketch);
        }
        {
            var Q0;
            Q0=makeQuery(id+"F6.imprint","IMPRINT",FACE,{"disambiguationData":[TD([[makeQuery(id+"F6.imprint","IMPRINT",EDGE,{"derivedFrom":sQuery(id+"F6.wireOp",EDGE,"E140.bottom")}),1.0]])]});
            var Q1;
            Q1=makeQuery(id+"F6.imprint","IMPRINT",FACE,{"disambiguationData":[TD([[makeQuery(id+"F6.imprint","IMPRINT",EDGE,{"derivedFrom":sQuery(id+"F6.wireOp",EDGE,"E142.bottom")}),-1.0]])]});
            extrude(context, id + "F7", {"entities" : qUnion([Q0, Q1]), "operationType" : NewBodyOperationType.REMOVE, "oppositeDirection" : true, "depth" : 3.8 * mm});
        }
        {
            var Q0;
            Q0=makeQuery(id+"F6.imprint","IMPRINT",FACE,{"disambiguationData":[TD([[makeQuery(id+"F6.imprint","IMPRINT",EDGE,{"derivedFrom":sQuery(id+"F6.wireOp",EDGE,"E143.bottom")}),-1.0]])]});
            var Q1;
            Q1=makeQuery(id+"F6.imprint","IMPRINT",FACE,{"disambiguationData":[TD([[makeQuery(id+"F6.imprint","IMPRINT",EDGE,{"derivedFrom":sQuery(id+"F6.wireOp",EDGE,"E141.bottom")}),-1.0]])]});
            var Q2;
            Q2=makeQuery(id+"F6.imprint","IMPRINT",FACE,{"disambiguationData":[TD([[makeQuery(id+"F6.imprint","IMPRINT",EDGE,{"derivedFrom":sQuery(id+"F6.wireOp",EDGE,"E144.bottom")}),1.0]])]});
            var Q3;
            Q3=makeQuery(id+"F6.imprint","IMPRINT",FACE,{"disambiguationData":[TD([[makeQuery(id+"F6.imprint","IMPRINT",EDGE,{"derivedFrom":sQuery(id+"F6.wireOp",EDGE,"E141.bottom")}),1.0]])]});
            extrude(context, id + "F8", {"entities" : qUnion([Q0, Q1, Q2, Q3]), "operationType" : NewBodyOperationType.REMOVE, "oppositeDirection" : true, "depth" : 6.35 * mm});
        }
        {
            var Q0;
            Q0=makeQuery(id+"F6.imprint","IMPRINT",FACE,{"disambiguationData":[TD([[makeQuery(id+"F6.imprint","IMPRINT",EDGE,{"derivedFrom":sQuery(id+"F6.wireOp",EDGE,"E141.bottom")}),-1.0]])]});
            extrude(context, id + "F9", {"entities" : qUnion([Q0]), "operationType" : NewBodyOperationType.ADD, "oppositeDirection" : true, "depth" : 3.8 * mm});
        }
        {
            var Q0;
            {var subQ1=sQuery(id+"F0.wireOp",EDGE,"E54.MirrorCS");Q0=makeQuery(id+"F0.imprint","IMPRINT",FACE,{"disambiguationData":[TD([[makeQuery(id+"F0.imprint","IMPRINT",EDGE,{"derivedFrom":subQ1}),-1.0]])]});}
            extrude(context, id + "F10", {"entities" : qUnion([Q0]), "operationType" : NewBodyOperationType.ADD, "depth" : 38.1 * mm});
        }
    });
